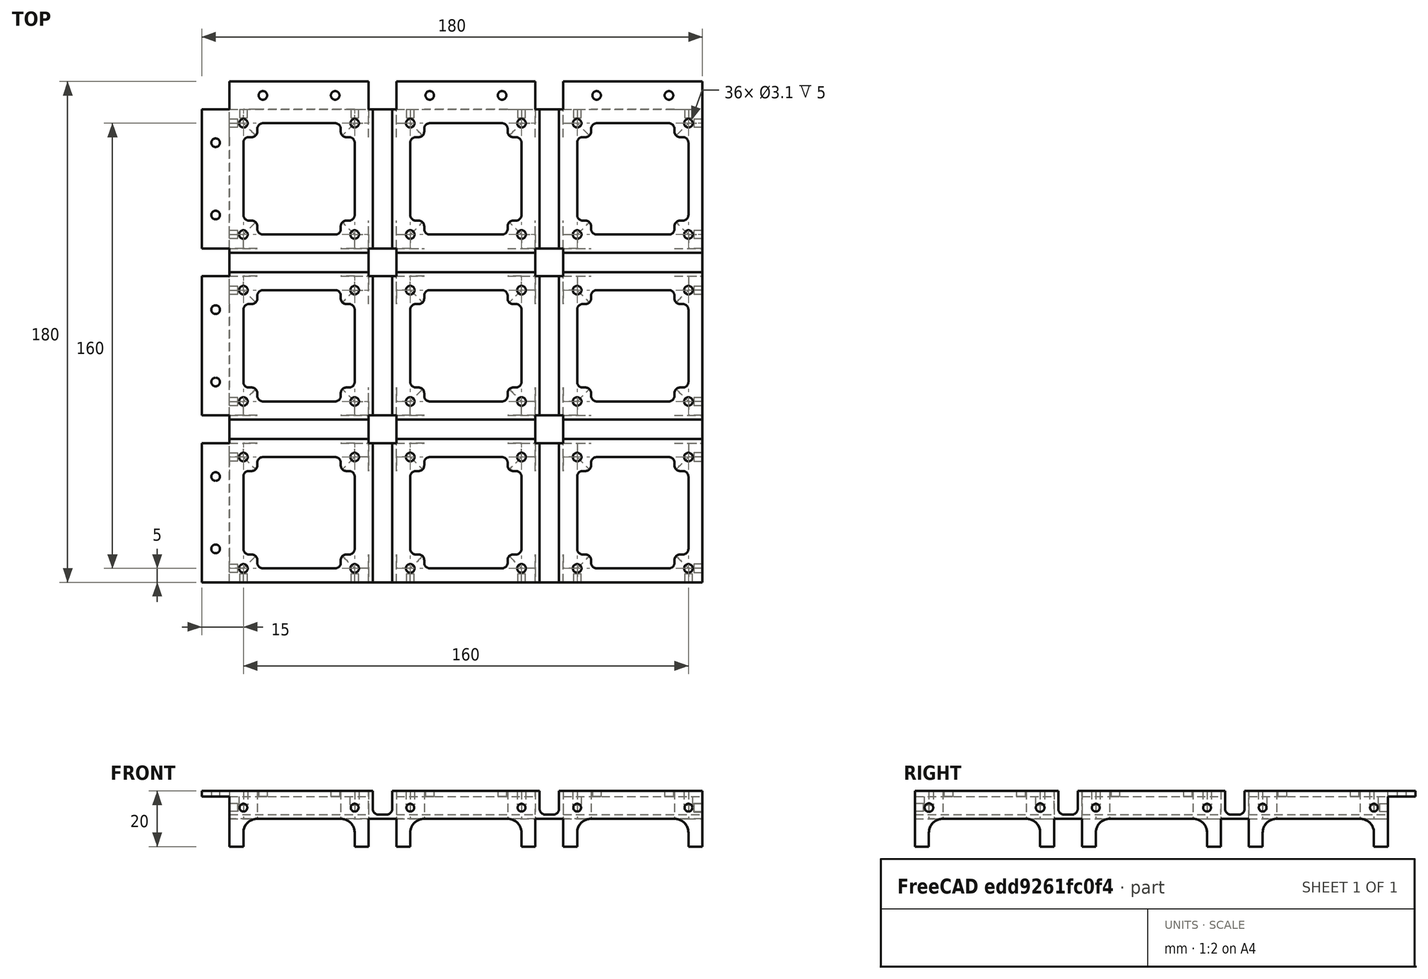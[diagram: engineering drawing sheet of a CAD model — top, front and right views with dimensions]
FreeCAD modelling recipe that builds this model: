
FCSTD DOCUMENT  (FreeCAD 0.20R29603 (Git))
Label: Backplane
License: All rights reserved
LicenseURL: http://en.wikipedia.org/wiki/All_rights_reserved
objects: Sketcher::SketchObject×59, PartDesign::Pocket×49, App::Link×16, PartDesign::Pad×10, PartDesign::Body×10, Part::Cylinder×2, Part::Cut×2, Part::Box×1, App::Part×1, Part::MultiFuse×1, Mesh::Feature×1
note: 193 computed .brp shape members not serialized (recipe doc carries the construction recipe); baked Part::Feature solids carry a one-line shape summary decoded from their .brp

FEATURE [Sketcher::SketchObject] Sketch
  FullyConstrained = true
  MapMode = 5
  Placement = pos=(0,0,0) rot=(0.57735,0.57735,0.57735;2.0944rad)
  Support = -> [YZ_Plane001]
  sketch-geometry (4):
    g0: LineSegment StartX=0 StartY=0 StartZ=0 EndX=10 EndY=0 EndZ=0
    g1: LineSegment StartX=10 StartY=0 StartZ=0 EndX=10 EndY=10 EndZ=0
    g2: LineSegment StartX=10 StartY=10 StartZ=0 EndX=0 EndY=10 EndZ=0
    g3: LineSegment StartX=0 StartY=10 StartZ=0 EndX=0 EndY=0 EndZ=0
  constraints (11):
    c: Coincident(g0,g1)
    c: Coincident(g1,g2)
    c: Coincident(g2,g3)
    c: Coincident(g3,g0)
    c: Horizontal(g0)
    c: Horizontal(g2)
    c: Vertical(g1)
    c: Vertical(g3)
    c: Coincident(g0,g-1)
    c: DistanceY(g3,g3) = 10
    c: DistanceX(g2,g2) = 10
FEATURE [PartDesign::Pad] Pad
  Direction = (1,-2e-16,3e-16)
  Length = 50
  Length2 = 10
  Placement = pos=(0,0,0) rot=(0.57735,0.57735,0.57735;2.0944rad)
  Profile = -> Sketch
  ReferenceAxis = -> Sketch [N_Axis]
  Type = 0
FEATURE [Sketcher::SketchObject] Sketch001
  ExternalGeometry = -> [Pad]
  FullyConstrained = true
  MapMode = 5
  Placement = pos=(0,0,0) rot=(0.57735,0.57735,-0.57735;4.18879rad)
  Support = -> [Pad]
  sketch-geometry (6):
    g0: LineSegment StartX=8.5 StartY=-10 StartZ=0 EndX=8.5 EndY=-3.5 EndZ=0
    g1: LineSegment StartX=6.5 StartY=-1.5 StartZ=0 EndX=3.5 EndY=-1.5 EndZ=0
    g2: LineSegment StartX=1.5 StartY=-3.5 StartZ=0 EndX=1.5 EndY=-10 EndZ=0
    g3: ArcOfCircle CenterX=6.5 CenterY=-3.5 CenterZ=0 NormalX=0 NormalY=0 NormalZ=1 AngleXU=0 Radius=2 StartAngle=1e-16 EndAngle=1.5708
    g4: ArcOfCircle CenterX=3.5 CenterY=-3.5 CenterZ=0 NormalX=0 NormalY=0 NormalZ=1 AngleXU=0 Radius=2 StartAngle=1.5708 EndAngle=3.14159
    g5: LineSegment StartX=1.5 StartY=-10 StartZ=0 EndX=8.5 EndY=-10 EndZ=0
  constraints (16):
    c: PointOnObject(g0,g-3)
    c: Vertical(g0)
    c: Horizontal(g1)
    c: PointOnObject(g2,g-3)
    c: Vertical(g2)
    c: Tangent(g0,g3) = -1.5708
    c: Tangent(g1,g3) = -1.5708
    c: Tangent(g1,g4) = -1.5708
    c: Tangent(g2,g4) = -1.5708
    c: Radius(g4) = 2
    c: Radius(g3) = 2
    c: Distance(g2,g-5) = 1.5
    c: Distance(g0,g-4) = 1.5
    c: Distance(g1,g-6) = 1.5
    c: Coincident(g5,g2)
    c: Coincident(g5,g0)
FEATURE [PartDesign::Pocket] Pocket
  BaseFeature = -> Pad
  Direction = (1,-4e-16,4e-16)
  Length = 5
  Length2 = 5
  Placement = pos=(0,0,0) rot=(0.57735,0.57735,0.57735;2.0944rad)
  Profile = -> Sketch001
  ReferenceAxis = -> Sketch001 [N_Axis]
  Type = 1
FEATURE [PartDesign::Body] Body  label="BackplaneChannel"
  Group = -> [Sketch,Pad,Sketch001,Pocket]
  Origin = -> Origin001
  Placement = pos=(0,50,10) rot=(0,0,1;0rad)
  Tip = -> Pocket
FEATURE [App::Link] Link008  label="BackplaneChannel001"
  LinkPlacement = pos=(60,50,10) rot=(0,0,1;0rad)
  LinkedObject = -> Body
  Placement = pos=(60,50,10) rot=(0,0,1;0rad)
FEATURE [App::Link] Link009  label="BackplaneChannel002"
  LinkPlacement = pos=(120,50,10) rot=(0,0,1;0rad)
  LinkedObject = -> Body
  Placement = pos=(120,50,10) rot=(0,0,1;0rad)
FEATURE [App::Link] Link010  label="BackplaneChannel003"
  LinkPlacement = pos=(0,110,10) rot=(0,0,1;0rad)
  LinkedObject = -> Body
  Placement = pos=(0,110,10) rot=(0,0,1;0rad)
FEATURE [App::Link] Link011  label="BackplaneChannel004"
  LinkPlacement = pos=(60,110,10) rot=(0,0,1;0rad)
  LinkedObject = -> Body
  Placement = pos=(60,110,10) rot=(0,0,1;0rad)
FEATURE [App::Link] Link012  label="BackplaneChannel005"
  LinkPlacement = pos=(120,110,10) rot=(0,0,1;0rad)
  LinkedObject = -> Body
  Placement = pos=(120,110,10) rot=(0,0,1;0rad)
FEATURE [App::Link] Link013  label="BackplaneChannel006"
  LinkPlacement = pos=(60,0,10) rot=(0,0,1;1.5708rad)
  LinkedObject = -> Body
  Placement = pos=(60,0,10) rot=(0,0,1;1.5708rad)
FEATURE [App::Link] Link014  label="BackplaneChannel007"
  LinkPlacement = pos=(120,0,10) rot=(0,0,1;1.5708rad)
  LinkedObject = -> Body
  Placement = pos=(120,0,10) rot=(0,0,1;1.5708rad)
FEATURE [App::Link] Link015  label="BackplaneChannel008"
  LinkPlacement = pos=(60,60,10) rot=(0,0,1;1.5708rad)
  LinkedObject = -> Body
  Placement = pos=(60,60,10) rot=(0,0,1;1.5708rad)
FEATURE [App::Link] Link016  label="BackplaneChannel009"
  LinkPlacement = pos=(60,120,10) rot=(0,0,1;1.5708rad)
  LinkedObject = -> Body
  Placement = pos=(60,120,10) rot=(0,0,1;1.5708rad)
FEATURE [App::Link] Link017  label="BackplaneChannel010"
  LinkPlacement = pos=(120,60,10) rot=(0,0,1;1.5708rad)
  LinkedObject = -> Body
  Placement = pos=(120,60,10) rot=(0,0,1;1.5708rad)
FEATURE [App::Link] Link018  label="BackplaneChannel011"
  LinkPlacement = pos=(120,120,10) rot=(0,0,1;1.5708rad)
  LinkedObject = -> Body
  Placement = pos=(120,120,10) rot=(0,0,1;1.5708rad)
FEATURE [Sketcher::SketchObject] Sketch002
  FullyConstrained = true
  MapMode = 5
  Support = -> [XY_Plane002]
  sketch-geometry (4):
    g0: LineSegment StartX=-25 StartY=25 StartZ=0 EndX=25 EndY=25 EndZ=0
    g1: LineSegment StartX=25 StartY=25 StartZ=0 EndX=25 EndY=-25 EndZ=0
    g2: LineSegment StartX=25 StartY=-25 StartZ=0 EndX=-25 EndY=-25 EndZ=0
    g3: LineSegment StartX=-25 StartY=-25 StartZ=0 EndX=-25 EndY=25 EndZ=0
  constraints (10):
    c: Coincident(g0,g1)
    c: Coincident(g1,g2)
    c: Coincident(g2,g3)
    c: Coincident(g3,g0)
    c: Horizontal(g0)
    c: Vertical(g3)
    c: Symmetric(g2,g1,g-2)
    c: Symmetric(g1,g0,g-1)
    c: DistanceY(g1,g1) = 50
    c: DistanceX(g2,g2) = 50
FEATURE [PartDesign::Pad] Pad001
  Direction = (0,0,1)
  Length = 20
  Length2 = 10
  Profile = -> Sketch002
  ReferenceAxis = -> Sketch002 [N_Axis]
  Type = 0
FEATURE [Sketcher::SketchObject] Sketch003
  ExternalGeometry = -> [Pad001]
  FullyConstrained = true
  MapMode = 5
  Placement = pos=(0,0,20) rot=(0,0,1;0rad)
  Support = -> [Pad001]
  sketch-geometry (36):
    g0: LineSegment StartX=-18 StartY=15 StartZ=0 EndX=-17 EndY=15 EndZ=0
    g1: LineSegment StartX=20 StartY=13 StartZ=0 EndX=20 EndY=-13 EndZ=0
    g2: LineSegment StartX=18 StartY=-15 StartZ=0 EndX=17 EndY=-15 EndZ=0
    g3: LineSegment StartX=-20 StartY=-13 StartZ=0 EndX=-20 EndY=13 EndZ=0
    g4: LineSegment StartX=-13 StartY=20 StartZ=0 EndX=13 EndY=20 EndZ=0
    g5: LineSegment StartX=15 StartY=18 StartZ=0 EndX=15 EndY=17 EndZ=0
    g6: LineSegment StartX=13 StartY=-20 StartZ=0 EndX=-13 EndY=-20 EndZ=0
    g7: LineSegment StartX=-15 StartY=-18 StartZ=0 EndX=-15 EndY=-17 EndZ=0
    g8: LineSegment StartX=17 StartY=15 StartZ=0 EndX=18 EndY=15 EndZ=0
    g9: LineSegment StartX=-15 StartY=17 StartZ=0 EndX=-15 EndY=18 EndZ=0
    g10: LineSegment StartX=-17 StartY=-15 StartZ=0 EndX=-18 EndY=-15 EndZ=0
    g11: LineSegment StartX=15 StartY=-17 StartZ=0 EndX=15 EndY=-18 EndZ=0
    g12: ArcOfCircle CenterX=-13 CenterY=-18 CenterZ=0 NormalX=0 NormalY=0 NormalZ=1 AngleXU=0 Radius=2 StartAngle=3.14159 EndAngle=4.71239
    g13: GeomPoint X=-15 Y=-20 Z=0
    g14: ArcOfCircle CenterX=13 CenterY=-18 CenterZ=0 NormalX=0 NormalY=0 NormalZ=1 AngleXU=0 Radius=2 StartAngle=4.71239 EndAngle=6.28319
    g15: GeomPoint X=15 Y=-20 Z=0
    g16: ArcOfCircle CenterX=17 CenterY=-17 CenterZ=0 NormalX=0 NormalY=0 NormalZ=1 AngleXU=0 Radius=2 StartAngle=1.5708 EndAngle=3.14159
    g17: GeomPoint X=15 Y=-15 Z=0
    g18: ArcOfCircle CenterX=18 CenterY=-13 CenterZ=0 NormalX=0 NormalY=0 NormalZ=1 AngleXU=0 Radius=2 StartAngle=4.71239 EndAngle=6.28319
    g19: GeomPoint X=20 Y=-15 Z=0
    g20: ArcOfCircle CenterX=18 CenterY=13 CenterZ=0 NormalX=0 NormalY=0 NormalZ=1 AngleXU=0 Radius=2 StartAngle=0 EndAngle=1.5708
    g21: GeomPoint X=20 Y=15 Z=0
    g22: ArcOfCircle CenterX=17 CenterY=17 CenterZ=0 NormalX=0 NormalY=0 NormalZ=1 AngleXU=0 Radius=2 StartAngle=3.14159 EndAngle=4.71239
    g23: GeomPoint X=15 Y=15 Z=0
    g24: ArcOfCircle CenterX=13 CenterY=18 CenterZ=0 NormalX=0 NormalY=0 NormalZ=1 AngleXU=0 Radius=2 StartAngle=4e-16 EndAngle=1.5708
    g25: GeomPoint X=15 Y=20 Z=0
    g26: ArcOfCircle CenterX=-13 CenterY=18 CenterZ=0 NormalX=0 NormalY=0 NormalZ=1 AngleXU=0 Radius=2 StartAngle=1.5708 EndAngle=3.14159
    g27: GeomPoint X=-15 Y=20 Z=0
    g28: ArcOfCircle CenterX=-17 CenterY=17 CenterZ=0 NormalX=0 NormalY=0 NormalZ=1 AngleXU=0 Radius=2 StartAngle=4.71239 EndAngle=6.28319
    g29: GeomPoint X=-15 Y=15 Z=0
    g30: ArcOfCircle CenterX=-18 CenterY=13 CenterZ=0 NormalX=0 NormalY=0 NormalZ=1 AngleXU=0 Radius=2 StartAngle=1.5708 EndAngle=3.14159
    g31: GeomPoint X=-20 Y=15 Z=0
    g32: ArcOfCircle CenterX=-18 CenterY=-13 CenterZ=0 NormalX=0 NormalY=0 NormalZ=1 AngleXU=0 Radius=2 StartAngle=3.14159 EndAngle=4.71239
    g33: GeomPoint X=-20 Y=-15 Z=0
    g34: ArcOfCircle CenterX=-17 CenterY=-17 CenterZ=0 NormalX=0 NormalY=0 NormalZ=1 AngleXU=0 Radius=2 StartAngle=0 EndAngle=1.5708
    g35: GeomPoint X=-15 Y=-15 Z=0
  constraints (80):
    c: Horizontal(g2)
    c: Vertical(g3)
    c: Symmetric(g21,g31,g-2)
    c: Symmetric(g21,g19,g-1)
    c: DistanceX(g31,g21) = 40
    c: DistanceY(g19,g21) = 30
    c: Horizontal(g4)
    c: Vertical(g7)
    c: Symmetric(g13,g15,g-2)
    c: Symmetric(g15,g25,g-1)
    c: DistanceY(g15,g25) = 40
    c: Vertical(g9)
    c: Vertical(g5)
    c: Vertical(g11)
    c: Horizontal(g10)
    c: Horizontal(g8)
    c: Horizontal(g0)
    c: DistanceX(g13,g15) = 30
    c: DistanceY(g33,g31) = 30
    c: DistanceX(g27,g25) = 30
    c: PointOnObject(g13,g7)
    c: PointOnObject(g13,g6)
    c: Tangent(g7,g12) = 1.5708
    c: Tangent(g6,g12) = 1.5708
    c: Radius(g12) = 2
    c: PointOnObject(g15,g11)
    c: PointOnObject(g15,g6)
    c: Tangent(g11,g14) = 1.5708
    c: Tangent(g6,g14) = 1.5708
    c: PointOnObject(g17,g11)
    c: PointOnObject(g17,g2)
    c: Tangent(g11,g16) = -1.5708
    c: Tangent(g2,g16) = -1.5708
    c: PointOnObject(g19,g2)
    c: PointOnObject(g19,g1)
    c: Tangent(g2,g18) = 1.5708
    c: Tangent(g1,g18) = 1.5708
    c: PointOnObject(g21,g1)
    c: PointOnObject(g21,g8)
    c: Tangent(g1,g20) = 1.5708
    c: Tangent(g8,g20) = 1.5708
    c: PointOnObject(g23,g8)
    c: PointOnObject(g23,g5)
    c: Tangent(g8,g22) = -1.5708
    c: Tangent(g5,g22) = -1.5708
    c: PointOnObject(g25,g5)
    c: PointOnObject(g25,g4)
    c: Tangent(g5,g24) = 1.5708
    c: Tangent(g4,g24) = 1.5708
    c: PointOnObject(g27,g9)
    c: PointOnObject(g27,g4)
    c: Tangent(g9,g26) = 1.5708
    c: Tangent(g4,g26) = 1.5708
    c: PointOnObject(g29,g9)
    c: PointOnObject(g29,g0)
    c: Tangent(g9,g28) = -1.5708
    c: Tangent(g0,g28) = -1.5708
    c: PointOnObject(g31,g0)
    c: PointOnObject(g31,g3)
    c: Tangent(g0,g30) = 1.5708
    c: Tangent(g3,g30) = 1.5708
    c: PointOnObject(g33,g3)
    c: PointOnObject(g33,g10)
    c: Tangent(g3,g32) = 1.5708
    c: Tangent(g10,g32) = 1.5708
    c: PointOnObject(g35,g10)
    c: PointOnObject(g35,g7)
    c: Tangent(g10,g34) = -1.5708
    c: Tangent(g7,g34) = -1.5708
    c: Radius(g34) = 2
    c: Radius(g32) = 2
    c: Radius(g30) = 2
    c: Radius(g28) = 2
    c: Radius(g26) = 2
    c: Radius(g24) = 2
    c: Radius(g22) = 2
    c: Radius(g20) = 2
    c: Radius(g18) = 2
    c: Radius(g16) = 2
    c: Radius(g14) = 2
FEATURE [PartDesign::Pocket] Pocket001
  BaseFeature = -> Pad001
  Direction = (0,0,-1)
  Length = 5
  Length2 = 5
  Profile = -> Sketch003
  ReferenceAxis = -> Sketch003 [N_Axis]
  Type = 1
FEATURE [Sketcher::SketchObject] Sketch004
  ExternalGeometry = -> [Pocket001]
  FullyConstrained = true
  MapMode = 5
  Placement = pos=(25,0,0) rot=(0.57735,0.57735,0.57735;2.0944rad)
  Support = -> [Pocket001]
  sketch-geometry (6):
    g0: LineSegment StartX=-15 StartY=10 StartZ=0 EndX=15 EndY=10 EndZ=0
    g1: LineSegment StartX=20 StartY=5 StartZ=0 EndX=20 EndY=0 EndZ=0
    g2: LineSegment StartX=20 StartY=0 StartZ=0 EndX=-20 EndY=0 EndZ=0
    g3: LineSegment StartX=-20 StartY=0 StartZ=0 EndX=-20 EndY=5 EndZ=0
    g4: ArcOfCircle CenterX=15 CenterY=5 CenterZ=0 NormalX=0 NormalY=0 NormalZ=1 AngleXU=0 Radius=5 StartAngle=1.11001e-11 EndAngle=1.5708
    g5: ArcOfCircle CenterX=-15 CenterY=5 CenterZ=0 NormalX=0 NormalY=0 NormalZ=1 AngleXU=0 Radius=5 StartAngle=1.5708 EndAngle=3.14159
  constraints (15):
    c: Coincident(g1,g2)
    c: Coincident(g2,g3)
    c: Vertical(g1)
    c: Vertical(g3)
    c: PointOnObject(g1,g-1)
    c: Tangent(g1,g4) = 1.5708
    c: Tangent(g0,g4) = 1.5708
    c: Tangent(g0,g5) = 1.5708
    c: Tangent(g3,g5) = 1.5708
    c: Horizontal(g0)
    c: DistanceX(g2,g2) = 40
    c: Symmetric(g2,g1,g-2)
    c: Distance(g-1,g0) = 10
    c: Radius(g5) = 5
    c: Radius(g4) = 5
FEATURE [PartDesign::Pocket] Pocket002
  BaseFeature = -> Pocket001
  Direction = (-1,0,0)
  Length = 5
  Length2 = 5
  Profile = -> Sketch004
  ReferenceAxis = -> Sketch004 [N_Axis]
  Type = 1
FEATURE [Sketcher::SketchObject] Sketch005
  FullyConstrained = true
  MapMode = 5
  Placement = pos=(0,-25,0) rot=(1,0,0;1.5708rad)
  Support = -> [Pocket001]
  sketch-geometry (6):
    g0: LineSegment StartX=-15 StartY=10 StartZ=0 EndX=15 EndY=10 EndZ=0
    g1: LineSegment StartX=20 StartY=5 StartZ=0 EndX=20 EndY=0 EndZ=0
    g2: LineSegment StartX=20 StartY=0 StartZ=0 EndX=-20 EndY=0 EndZ=0
    g3: LineSegment StartX=-20 StartY=0 StartZ=0 EndX=-20 EndY=5 EndZ=0
    g4: ArcOfCircle CenterX=15 CenterY=5 CenterZ=0 NormalX=0 NormalY=0 NormalZ=1 AngleXU=0 Radius=5 StartAngle=1.11e-11 EndAngle=1.5708
    g5: ArcOfCircle CenterX=-15 CenterY=5 CenterZ=0 NormalX=0 NormalY=0 NormalZ=1 AngleXU=0 Radius=5 StartAngle=1.5708 EndAngle=3.14159
  constraints (15):
    c: Coincident(g1,g2)
    c: Coincident(g2,g3)
    c: Horizontal(g0)
    c: Vertical(g1)
    c: Vertical(g3)
    c: Symmetric(g2,g1,g-2)
    c: PointOnObject(g1,g-1)
    c: Tangent(g0,g4) = 1.5708
    c: Tangent(g1,g4) = 1.5708
    c: Tangent(g0,g5) = 1.5708
    c: Tangent(g3,g5) = 1.5708
    c: DistanceX(g2,g2) = 40
    c: Distance(g-1,g0) = 10
    c: Radius(g5) = 5
    c: Radius(g4) = 5
FEATURE [PartDesign::Pocket] Pocket003
  BaseFeature = -> Pocket002
  Direction = (0,1,-2e-16)
  Length = 5
  Length2 = 5
  Profile = -> Sketch005
  ReferenceAxis = -> Sketch005 [N_Axis]
  Type = 1
FEATURE [Sketcher::SketchObject] Sketch009
  FullyConstrained = false
  MapMode = 5
  Placement = pos=(0,0,20) rot=(0,0,1;0rad)
  sketch-geometry (4):
    g0: Circle CenterX=-20 CenterY=20 CenterZ=0 NormalX=0 NormalY=0 NormalZ=1 AngleXU=0 Radius=1.55
    g1: Circle CenterX=20 CenterY=20 CenterZ=0 NormalX=0 NormalY=0 NormalZ=1 AngleXU=0 Radius=1.55
    g2: Circle CenterX=20 CenterY=-20 CenterZ=0 NormalX=0 NormalY=0 NormalZ=1 AngleXU=0 Radius=1.55
    g3: Circle CenterX=-20 CenterY=-20 CenterZ=0 NormalX=0 NormalY=0 NormalZ=1 AngleXU=0 Radius=1.55
  constraints (4):
    c: Diameter(g0) = 3.1
    c: Diameter(g1) = 3.1
    c: Diameter(g2) = 3.1
    c: Diameter(g3) = 3.1
FEATURE [PartDesign::Pocket] Pocket008
  BaseFeature = -> Pocket003
  Direction = (0,0,-1)
  Length = 5
  Length2 = 5
  Profile = -> Sketch009
  ReferenceAxis = -> Sketch009 [N_Axis]
  Type = 0
FEATURE [Sketcher::SketchObject] Sketch010
  FullyConstrained = true
  MapMode = 5
  Support = -> [XY_Plane003]
  sketch-geometry (4):
    g0: LineSegment StartX=-25 StartY=25 StartZ=0 EndX=25 EndY=25 EndZ=0
    g1: LineSegment StartX=25 StartY=25 StartZ=0 EndX=25 EndY=-25 EndZ=0
    g2: LineSegment StartX=25 StartY=-25 StartZ=0 EndX=-25 EndY=-25 EndZ=0
    g3: LineSegment StartX=-25 StartY=-25 StartZ=0 EndX=-25 EndY=25 EndZ=0
  constraints (10):
    c: Coincident(g0,g1)
    c: Coincident(g1,g2)
    c: Coincident(g2,g3)
    c: Coincident(g3,g0)
    c: Horizontal(g0)
    c: Vertical(g3)
    c: Symmetric(g2,g1,g-2)
    c: Symmetric(g1,g0,g-1)
    c: DistanceY(g1,g1) = 50
    c: DistanceX(g2,g2) = 50
FEATURE [PartDesign::Pad] Pad002
  Direction = (0,0,1)
  Length = 20
  Length2 = 10
  Profile = -> Sketch010
  ReferenceAxis = -> Sketch010 [N_Axis]
  Type = 0
FEATURE [Sketcher::SketchObject] Sketch011
  ExternalGeometry = -> [Pad002]
  FullyConstrained = true
  MapMode = 5
  Placement = pos=(0,0,20) rot=(0,0,1;0rad)
  Support = -> [Pad002]
  sketch-geometry (36):
    g0: LineSegment StartX=-18 StartY=15 StartZ=0 EndX=-17 EndY=15 EndZ=0
    g1: LineSegment StartX=20 StartY=13 StartZ=0 EndX=20 EndY=-13 EndZ=0
    g2: LineSegment StartX=18 StartY=-15 StartZ=0 EndX=17 EndY=-15 EndZ=0
    g3: LineSegment StartX=-20 StartY=-13 StartZ=0 EndX=-20 EndY=13 EndZ=0
    g4: LineSegment StartX=-13 StartY=20 StartZ=0 EndX=13 EndY=20 EndZ=0
    g5: LineSegment StartX=15 StartY=18 StartZ=0 EndX=15 EndY=17 EndZ=0
    g6: LineSegment StartX=13 StartY=-20 StartZ=0 EndX=-13 EndY=-20 EndZ=0
    g7: LineSegment StartX=-15 StartY=-18 StartZ=0 EndX=-15 EndY=-17 EndZ=0
    g8: LineSegment StartX=17 StartY=15 StartZ=0 EndX=18 EndY=15 EndZ=0
    g9: LineSegment StartX=-15 StartY=17 StartZ=0 EndX=-15 EndY=18 EndZ=0
    g10: LineSegment StartX=-17 StartY=-15 StartZ=0 EndX=-18 EndY=-15 EndZ=0
    g11: LineSegment StartX=15 StartY=-17 StartZ=0 EndX=15 EndY=-18 EndZ=0
    g12: ArcOfCircle CenterX=-13 CenterY=-18 CenterZ=0 NormalX=0 NormalY=0 NormalZ=1 AngleXU=0 Radius=2 StartAngle=3.14159 EndAngle=4.71239
    g13: GeomPoint X=-15 Y=-20 Z=0
    g14: ArcOfCircle CenterX=13 CenterY=-18 CenterZ=0 NormalX=0 NormalY=0 NormalZ=1 AngleXU=0 Radius=2 StartAngle=4.71239 EndAngle=6.28319
    g15: GeomPoint X=15 Y=-20 Z=0
    g16: ArcOfCircle CenterX=17 CenterY=-17 CenterZ=0 NormalX=0 NormalY=0 NormalZ=1 AngleXU=0 Radius=2 StartAngle=1.5708 EndAngle=3.14159
    g17: GeomPoint X=15 Y=-15 Z=0
    g18: ArcOfCircle CenterX=18 CenterY=-13 CenterZ=0 NormalX=0 NormalY=0 NormalZ=1 AngleXU=0 Radius=2 StartAngle=4.71239 EndAngle=6.28319
    g19: GeomPoint X=20 Y=-15 Z=0
    g20: ArcOfCircle CenterX=18 CenterY=13 CenterZ=0 NormalX=0 NormalY=0 NormalZ=1 AngleXU=0 Radius=2 StartAngle=0 EndAngle=1.5708
    g21: GeomPoint X=20 Y=15 Z=0
    g22: ArcOfCircle CenterX=17 CenterY=17 CenterZ=0 NormalX=0 NormalY=0 NormalZ=1 AngleXU=0 Radius=2 StartAngle=3.14159 EndAngle=4.71239
    g23: GeomPoint X=15 Y=15 Z=0
    g24: ArcOfCircle CenterX=13 CenterY=18 CenterZ=0 NormalX=0 NormalY=0 NormalZ=1 AngleXU=0 Radius=2 StartAngle=4e-16 EndAngle=1.5708
    g25: GeomPoint X=15 Y=20 Z=0
    g26: ArcOfCircle CenterX=-13 CenterY=18 CenterZ=0 NormalX=0 NormalY=0 NormalZ=1 AngleXU=0 Radius=2 StartAngle=1.5708 EndAngle=3.14159
    g27: GeomPoint X=-15 Y=20 Z=0
    g28: ArcOfCircle CenterX=-17 CenterY=17 CenterZ=0 NormalX=0 NormalY=0 NormalZ=1 AngleXU=0 Radius=2 StartAngle=4.71239 EndAngle=6.28319
    g29: GeomPoint X=-15 Y=15 Z=0
    g30: ArcOfCircle CenterX=-18 CenterY=13 CenterZ=0 NormalX=0 NormalY=0 NormalZ=1 AngleXU=0 Radius=2 StartAngle=1.5708 EndAngle=3.14159
    g31: GeomPoint X=-20 Y=15 Z=0
    g32: ArcOfCircle CenterX=-18 CenterY=-13 CenterZ=0 NormalX=0 NormalY=0 NormalZ=1 AngleXU=0 Radius=2 StartAngle=3.14159 EndAngle=4.71239
    g33: GeomPoint X=-20 Y=-15 Z=0
    g34: ArcOfCircle CenterX=-17 CenterY=-17 CenterZ=0 NormalX=0 NormalY=0 NormalZ=1 AngleXU=0 Radius=2 StartAngle=0 EndAngle=1.5708
    g35: GeomPoint X=-15 Y=-15 Z=0
  constraints (80):
    c: Horizontal(g2)
    c: Vertical(g3)
    c: Symmetric(g21,g31,g-2)
    c: Symmetric(g21,g19,g-1)
    c: DistanceX(g31,g21) = 40
    c: DistanceY(g19,g21) = 30
    c: Horizontal(g4)
    c: Vertical(g7)
    c: Symmetric(g13,g15,g-2)
    c: Symmetric(g15,g25,g-1)
    c: DistanceY(g15,g25) = 40
    c: Vertical(g9)
    c: Vertical(g5)
    c: Vertical(g11)
    c: Horizontal(g10)
    c: Horizontal(g8)
    c: Horizontal(g0)
    c: DistanceX(g13,g15) = 30
    c: DistanceY(g33,g31) = 30
    c: DistanceX(g27,g25) = 30
    c: PointOnObject(g13,g7)
    c: PointOnObject(g13,g6)
    c: Tangent(g7,g12) = 1.5708
    c: Tangent(g6,g12) = 1.5708
    c: Radius(g12) = 2
    c: PointOnObject(g15,g11)
    c: PointOnObject(g15,g6)
    c: Tangent(g11,g14) = 1.5708
    c: Tangent(g6,g14) = 1.5708
    c: PointOnObject(g17,g11)
    c: PointOnObject(g17,g2)
    c: Tangent(g11,g16) = -1.5708
    c: Tangent(g2,g16) = -1.5708
    c: PointOnObject(g19,g2)
    c: PointOnObject(g19,g1)
    c: Tangent(g2,g18) = 1.5708
    c: Tangent(g1,g18) = 1.5708
    c: PointOnObject(g21,g1)
    c: PointOnObject(g21,g8)
    c: Tangent(g1,g20) = 1.5708
    c: Tangent(g8,g20) = 1.5708
    c: PointOnObject(g23,g8)
    c: PointOnObject(g23,g5)
    c: Tangent(g8,g22) = -1.5708
    c: Tangent(g5,g22) = -1.5708
    c: PointOnObject(g25,g5)
    c: PointOnObject(g25,g4)
    c: Tangent(g5,g24) = 1.5708
    c: Tangent(g4,g24) = 1.5708
    c: PointOnObject(g27,g9)
    c: PointOnObject(g27,g4)
    c: Tangent(g9,g26) = 1.5708
    c: Tangent(g4,g26) = 1.5708
    c: PointOnObject(g29,g9)
    c: PointOnObject(g29,g0)
    c: Tangent(g9,g28) = -1.5708
    c: Tangent(g0,g28) = -1.5708
    c: PointOnObject(g31,g0)
    c: PointOnObject(g31,g3)
    c: Tangent(g0,g30) = 1.5708
    c: Tangent(g3,g30) = 1.5708
    c: PointOnObject(g33,g3)
    c: PointOnObject(g33,g10)
    c: Tangent(g3,g32) = 1.5708
    c: Tangent(g10,g32) = 1.5708
    c: PointOnObject(g35,g10)
    c: PointOnObject(g35,g7)
    c: Tangent(g10,g34) = -1.5708
    c: Tangent(g7,g34) = -1.5708
    c: Radius(g34) = 2
    c: Radius(g32) = 2
    c: Radius(g30) = 2
    c: Radius(g28) = 2
    c: Radius(g26) = 2
    c: Radius(g24) = 2
    c: Radius(g22) = 2
    c: Radius(g20) = 2
    c: Radius(g18) = 2
    c: Radius(g16) = 2
    c: Radius(g14) = 2
FEATURE [PartDesign::Pocket] Pocket009
  BaseFeature = -> Pad002
  Direction = (0,0,-1)
  Length = 5
  Length2 = 5
  Profile = -> Sketch011
  ReferenceAxis = -> Sketch011 [N_Axis]
  Type = 1
FEATURE [Sketcher::SketchObject] Sketch012
  ExternalGeometry = -> [Pocket009]
  FullyConstrained = true
  MapMode = 5
  Placement = pos=(25,0,0) rot=(0.57735,0.57735,0.57735;2.0944rad)
  Support = -> [Pocket009]
  sketch-geometry (6):
    g0: LineSegment StartX=-15 StartY=10 StartZ=0 EndX=15 EndY=10 EndZ=0
    g1: LineSegment StartX=20 StartY=5 StartZ=0 EndX=20 EndY=0 EndZ=0
    g2: LineSegment StartX=20 StartY=0 StartZ=0 EndX=-20 EndY=0 EndZ=0
    g3: LineSegment StartX=-20 StartY=0 StartZ=0 EndX=-20 EndY=5 EndZ=0
    g4: ArcOfCircle CenterX=15 CenterY=5 CenterZ=0 NormalX=0 NormalY=0 NormalZ=1 AngleXU=0 Radius=5 StartAngle=1.11001e-11 EndAngle=1.5708
    g5: ArcOfCircle CenterX=-15 CenterY=5 CenterZ=0 NormalX=0 NormalY=0 NormalZ=1 AngleXU=0 Radius=5 StartAngle=1.5708 EndAngle=3.14159
  constraints (15):
    c: Coincident(g1,g2)
    c: Coincident(g2,g3)
    c: Vertical(g1)
    c: Vertical(g3)
    c: PointOnObject(g1,g-1)
    c: Tangent(g1,g4) = 1.5708
    c: Tangent(g0,g4) = 1.5708
    c: Tangent(g0,g5) = 1.5708
    c: Tangent(g3,g5) = 1.5708
    c: Horizontal(g0)
    c: DistanceX(g2,g2) = 40
    c: Symmetric(g2,g1,g-2)
    c: Distance(g-1,g0) = 10
    c: Radius(g5) = 5
    c: Radius(g4) = 5
FEATURE [PartDesign::Pocket] Pocket010
  BaseFeature = -> Pocket009
  Direction = (-1,0,0)
  Length = 5
  Length2 = 5
  Profile = -> Sketch012
  ReferenceAxis = -> Sketch012 [N_Axis]
  Type = 1
FEATURE [Sketcher::SketchObject] Sketch013
  FullyConstrained = true
  MapMode = 5
  Placement = pos=(0,-25,0) rot=(1,0,0;1.5708rad)
  Support = -> [Pocket009]
  sketch-geometry (6):
    g0: LineSegment StartX=-15 StartY=10 StartZ=0 EndX=15 EndY=10 EndZ=0
    g1: LineSegment StartX=20 StartY=5 StartZ=0 EndX=20 EndY=0 EndZ=0
    g2: LineSegment StartX=20 StartY=0 StartZ=0 EndX=-20 EndY=0 EndZ=0
    g3: LineSegment StartX=-20 StartY=0 StartZ=0 EndX=-20 EndY=5 EndZ=0
    g4: ArcOfCircle CenterX=15 CenterY=5 CenterZ=0 NormalX=0 NormalY=0 NormalZ=1 AngleXU=0 Radius=5 StartAngle=1.11e-11 EndAngle=1.5708
    g5: ArcOfCircle CenterX=-15 CenterY=5 CenterZ=0 NormalX=0 NormalY=0 NormalZ=1 AngleXU=0 Radius=5 StartAngle=1.5708 EndAngle=3.14159
  constraints (15):
    c: Coincident(g1,g2)
    c: Coincident(g2,g3)
    c: Horizontal(g0)
    c: Vertical(g1)
    c: Vertical(g3)
    c: Symmetric(g2,g1,g-2)
    c: PointOnObject(g1,g-1)
    c: Tangent(g0,g4) = 1.5708
    c: Tangent(g1,g4) = 1.5708
    c: Tangent(g0,g5) = 1.5708
    c: Tangent(g3,g5) = 1.5708
    c: DistanceX(g2,g2) = 40
    c: Distance(g-1,g0) = 10
    c: Radius(g5) = 5
    c: Radius(g4) = 5
FEATURE [PartDesign::Pocket] Pocket011
  BaseFeature = -> Pocket010
  Direction = (0,1,-2e-16)
  Length = 5
  Length2 = 5
  Profile = -> Sketch013
  ReferenceAxis = -> Sketch013 [N_Axis]
  Type = 1
FEATURE [Sketcher::SketchObject] Sketch014
  FullyConstrained = false
  MapMode = 5
  Placement = pos=(0,0,20) rot=(0,0,1;0rad)
  sketch-geometry (4):
    g0: Circle CenterX=-20 CenterY=20 CenterZ=0 NormalX=0 NormalY=0 NormalZ=1 AngleXU=0 Radius=1.55
    g1: Circle CenterX=20 CenterY=20 CenterZ=0 NormalX=0 NormalY=0 NormalZ=1 AngleXU=0 Radius=1.55
    g2: Circle CenterX=20 CenterY=-20 CenterZ=0 NormalX=0 NormalY=0 NormalZ=1 AngleXU=0 Radius=1.55
    g3: Circle CenterX=-20 CenterY=-20 CenterZ=0 NormalX=0 NormalY=0 NormalZ=1 AngleXU=0 Radius=1.55
  constraints (4):
    c: Diameter(g0) = 3.1
    c: Diameter(g1) = 3.1
    c: Diameter(g2) = 3.1
    c: Diameter(g3) = 3.1
FEATURE [PartDesign::Pocket] Pocket012
  BaseFeature = -> Pocket011
  Direction = (0,0,-1)
  Length = 5
  Length2 = 5
  Profile = -> Sketch014
  ReferenceAxis = -> Sketch014 [N_Axis]
  Type = 0
FEATURE [PartDesign::Body] Body003  label="BackplaneBlock001"
  Group = -> [Sketch010,Pad002,Sketch011,Pocket009,Sketch012,Sketch013,Pocket010,Pocket011,Sketch014,Pocket012]
  Origin = -> Origin003
  Placement = pos=(85,85,0) rot=(0,0,1;0rad)
  Tip = -> Pocket012
FEATURE [Sketcher::SketchObject] Sketch015
  ExternalGeometry = -> [Pocket008]
  FullyConstrained = true
  MapMode = 5
  Placement = pos=(0,-25,0) rot=(1,0,0;1.5708rad)
  Support = -> [Pocket008]
  sketch-geometry (2):
    g0: Circle CenterX=-20 CenterY=14 CenterZ=0 NormalX=0 NormalY=0 NormalZ=1 AngleXU=0 Radius=1.4
    g1: Circle CenterX=20 CenterY=14 CenterZ=0 NormalX=0 NormalY=0 NormalZ=1 AngleXU=0 Radius=1.4
  constraints (6):
    c: Diameter(g0) = 2.8
    c: Diameter(g1) = 2.8
    c: Distance(g0,g-5) = 5
    c: Distance(g0,g-3) = 6
    c: Distance(g1,g-3) = 6
    c: Distance(g1,g-4) = 5
FEATURE [PartDesign::Pocket] Pocket013
  BaseFeature = -> Pocket008
  Direction = (0,1,-2e-16)
  Length = 3
  Length2 = 5
  Profile = -> Sketch015
  ReferenceAxis = -> Sketch015 [N_Axis]
  Type = 0
FEATURE [Sketcher::SketchObject] Sketch016
  FullyConstrained = true
  MapMode = 5
  Support = -> [XY_Plane004]
  sketch-geometry (4):
    g0: LineSegment StartX=-25 StartY=25 StartZ=0 EndX=25 EndY=25 EndZ=0
    g1: LineSegment StartX=25 StartY=25 StartZ=0 EndX=25 EndY=-25 EndZ=0
    g2: LineSegment StartX=25 StartY=-25 StartZ=0 EndX=-25 EndY=-25 EndZ=0
    g3: LineSegment StartX=-25 StartY=-25 StartZ=0 EndX=-25 EndY=25 EndZ=0
  constraints (10):
    c: Coincident(g0,g1)
    c: Coincident(g1,g2)
    c: Coincident(g2,g3)
    c: Coincident(g3,g0)
    c: Horizontal(g0)
    c: Vertical(g3)
    c: Symmetric(g2,g1,g-2)
    c: Symmetric(g1,g0,g-1)
    c: DistanceY(g1,g1) = 50
    c: DistanceX(g2,g2) = 50
FEATURE [PartDesign::Pad] Pad003
  Direction = (0,0,1)
  Length = 20
  Length2 = 10
  Profile = -> Sketch016
  ReferenceAxis = -> Sketch016 [N_Axis]
  Type = 0
FEATURE [Sketcher::SketchObject] Sketch017
  ExternalGeometry = -> [Pad003]
  FullyConstrained = true
  MapMode = 5
  Placement = pos=(0,0,20) rot=(0,0,1;0rad)
  Support = -> [Pad003]
  sketch-geometry (36):
    g0: LineSegment StartX=-18 StartY=15 StartZ=0 EndX=-17 EndY=15 EndZ=0
    g1: LineSegment StartX=20 StartY=13 StartZ=0 EndX=20 EndY=-13 EndZ=0
    g2: LineSegment StartX=18 StartY=-15 StartZ=0 EndX=17 EndY=-15 EndZ=0
    g3: LineSegment StartX=-20 StartY=-13 StartZ=0 EndX=-20 EndY=13 EndZ=0
    g4: LineSegment StartX=-13 StartY=20 StartZ=0 EndX=13 EndY=20 EndZ=0
    g5: LineSegment StartX=15 StartY=18 StartZ=0 EndX=15 EndY=17 EndZ=0
    g6: LineSegment StartX=13 StartY=-20 StartZ=0 EndX=-13 EndY=-20 EndZ=0
    g7: LineSegment StartX=-15 StartY=-18 StartZ=0 EndX=-15 EndY=-17 EndZ=0
    g8: LineSegment StartX=17 StartY=15 StartZ=0 EndX=18 EndY=15 EndZ=0
    g9: LineSegment StartX=-15 StartY=17 StartZ=0 EndX=-15 EndY=18 EndZ=0
    g10: LineSegment StartX=-17 StartY=-15 StartZ=0 EndX=-18 EndY=-15 EndZ=0
    g11: LineSegment StartX=15 StartY=-17 StartZ=0 EndX=15 EndY=-18 EndZ=0
    g12: ArcOfCircle CenterX=-13 CenterY=-18 CenterZ=0 NormalX=0 NormalY=0 NormalZ=1 AngleXU=0 Radius=2 StartAngle=3.14159 EndAngle=4.71239
    g13: GeomPoint X=-15 Y=-20 Z=0
    g14: ArcOfCircle CenterX=13 CenterY=-18 CenterZ=0 NormalX=0 NormalY=0 NormalZ=1 AngleXU=0 Radius=2 StartAngle=4.71239 EndAngle=6.28319
    g15: GeomPoint X=15 Y=-20 Z=0
    g16: ArcOfCircle CenterX=17 CenterY=-17 CenterZ=0 NormalX=0 NormalY=0 NormalZ=1 AngleXU=0 Radius=2 StartAngle=1.5708 EndAngle=3.14159
    g17: GeomPoint X=15 Y=-15 Z=0
    g18: ArcOfCircle CenterX=18 CenterY=-13 CenterZ=0 NormalX=0 NormalY=0 NormalZ=1 AngleXU=0 Radius=2 StartAngle=4.71239 EndAngle=6.28319
    g19: GeomPoint X=20 Y=-15 Z=0
    g20: ArcOfCircle CenterX=18 CenterY=13 CenterZ=0 NormalX=0 NormalY=0 NormalZ=1 AngleXU=0 Radius=2 StartAngle=0 EndAngle=1.5708
    g21: GeomPoint X=20 Y=15 Z=0
    g22: ArcOfCircle CenterX=17 CenterY=17 CenterZ=0 NormalX=0 NormalY=0 NormalZ=1 AngleXU=0 Radius=2 StartAngle=3.14159 EndAngle=4.71239
    g23: GeomPoint X=15 Y=15 Z=0
    g24: ArcOfCircle CenterX=13 CenterY=18 CenterZ=0 NormalX=0 NormalY=0 NormalZ=1 AngleXU=0 Radius=2 StartAngle=4e-16 EndAngle=1.5708
    g25: GeomPoint X=15 Y=20 Z=0
    g26: ArcOfCircle CenterX=-13 CenterY=18 CenterZ=0 NormalX=0 NormalY=0 NormalZ=1 AngleXU=0 Radius=2 StartAngle=1.5708 EndAngle=3.14159
    g27: GeomPoint X=-15 Y=20 Z=0
    g28: ArcOfCircle CenterX=-17 CenterY=17 CenterZ=0 NormalX=0 NormalY=0 NormalZ=1 AngleXU=0 Radius=2 StartAngle=4.71239 EndAngle=6.28319
    g29: GeomPoint X=-15 Y=15 Z=0
    g30: ArcOfCircle CenterX=-18 CenterY=13 CenterZ=0 NormalX=0 NormalY=0 NormalZ=1 AngleXU=0 Radius=2 StartAngle=1.5708 EndAngle=3.14159
    g31: GeomPoint X=-20 Y=15 Z=0
    g32: ArcOfCircle CenterX=-18 CenterY=-13 CenterZ=0 NormalX=0 NormalY=0 NormalZ=1 AngleXU=0 Radius=2 StartAngle=3.14159 EndAngle=4.71239
    g33: GeomPoint X=-20 Y=-15 Z=0
    g34: ArcOfCircle CenterX=-17 CenterY=-17 CenterZ=0 NormalX=0 NormalY=0 NormalZ=1 AngleXU=0 Radius=2 StartAngle=0 EndAngle=1.5708
    g35: GeomPoint X=-15 Y=-15 Z=0
  constraints (80):
    c: Horizontal(g2)
    c: Vertical(g3)
    c: Symmetric(g21,g31,g-2)
    c: Symmetric(g21,g19,g-1)
    c: DistanceX(g31,g21) = 40
    c: DistanceY(g19,g21) = 30
    c: Horizontal(g4)
    c: Vertical(g7)
    c: Symmetric(g13,g15,g-2)
    c: Symmetric(g15,g25,g-1)
    c: DistanceY(g15,g25) = 40
    c: Vertical(g9)
    c: Vertical(g5)
    c: Vertical(g11)
    c: Horizontal(g10)
    c: Horizontal(g8)
    c: Horizontal(g0)
    c: DistanceX(g13,g15) = 30
    c: DistanceY(g33,g31) = 30
    c: DistanceX(g27,g25) = 30
    c: PointOnObject(g13,g7)
    c: PointOnObject(g13,g6)
    c: Tangent(g7,g12) = 1.5708
    c: Tangent(g6,g12) = 1.5708
    c: Radius(g12) = 2
    c: PointOnObject(g15,g11)
    c: PointOnObject(g15,g6)
    c: Tangent(g11,g14) = 1.5708
    c: Tangent(g6,g14) = 1.5708
    c: PointOnObject(g17,g11)
    c: PointOnObject(g17,g2)
    c: Tangent(g11,g16) = -1.5708
    c: Tangent(g2,g16) = -1.5708
    c: PointOnObject(g19,g2)
    c: PointOnObject(g19,g1)
    c: Tangent(g2,g18) = 1.5708
    c: Tangent(g1,g18) = 1.5708
    c: PointOnObject(g21,g1)
    c: PointOnObject(g21,g8)
    c: Tangent(g1,g20) = 1.5708
    c: Tangent(g8,g20) = 1.5708
    c: PointOnObject(g23,g8)
    c: PointOnObject(g23,g5)
    c: Tangent(g8,g22) = -1.5708
    c: Tangent(g5,g22) = -1.5708
    c: PointOnObject(g25,g5)
    c: PointOnObject(g25,g4)
    c: Tangent(g5,g24) = 1.5708
    c: Tangent(g4,g24) = 1.5708
    c: PointOnObject(g27,g9)
    c: PointOnObject(g27,g4)
    c: Tangent(g9,g26) = 1.5708
    c: Tangent(g4,g26) = 1.5708
    c: PointOnObject(g29,g9)
    c: PointOnObject(g29,g0)
    c: Tangent(g9,g28) = -1.5708
    c: Tangent(g0,g28) = -1.5708
    c: PointOnObject(g31,g0)
    c: PointOnObject(g31,g3)
    c: Tangent(g0,g30) = 1.5708
    c: Tangent(g3,g30) = 1.5708
    c: PointOnObject(g33,g3)
    c: PointOnObject(g33,g10)
    c: Tangent(g3,g32) = 1.5708
    c: Tangent(g10,g32) = 1.5708
    c: PointOnObject(g35,g10)
    c: PointOnObject(g35,g7)
    c: Tangent(g10,g34) = -1.5708
    c: Tangent(g7,g34) = -1.5708
    c: Radius(g34) = 2
    c: Radius(g32) = 2
    c: Radius(g30) = 2
    c: Radius(g28) = 2
    c: Radius(g26) = 2
    c: Radius(g24) = 2
    c: Radius(g22) = 2
    c: Radius(g20) = 2
    c: Radius(g18) = 2
    c: Radius(g16) = 2
    c: Radius(g14) = 2
FEATURE [PartDesign::Pocket] Pocket014
  BaseFeature = -> Pad003
  Direction = (0,0,-1)
  Length = 5
  Length2 = 5
  Profile = -> Sketch017
  ReferenceAxis = -> Sketch017 [N_Axis]
  Type = 1
FEATURE [Sketcher::SketchObject] Sketch018
  ExternalGeometry = -> [Pocket014]
  FullyConstrained = true
  MapMode = 5
  Placement = pos=(25,0,0) rot=(0.57735,0.57735,0.57735;2.0944rad)
  Support = -> [Pocket014]
  sketch-geometry (6):
    g0: LineSegment StartX=-15 StartY=10 StartZ=0 EndX=15 EndY=10 EndZ=0
    g1: LineSegment StartX=20 StartY=5 StartZ=0 EndX=20 EndY=0 EndZ=0
    g2: LineSegment StartX=20 StartY=0 StartZ=0 EndX=-20 EndY=0 EndZ=0
    g3: LineSegment StartX=-20 StartY=0 StartZ=0 EndX=-20 EndY=5 EndZ=0
    g4: ArcOfCircle CenterX=15 CenterY=5 CenterZ=0 NormalX=0 NormalY=0 NormalZ=1 AngleXU=0 Radius=5 StartAngle=1.11001e-11 EndAngle=1.5708
    g5: ArcOfCircle CenterX=-15 CenterY=5 CenterZ=0 NormalX=0 NormalY=0 NormalZ=1 AngleXU=0 Radius=5 StartAngle=1.5708 EndAngle=3.14159
  constraints (15):
    c: Coincident(g1,g2)
    c: Coincident(g2,g3)
    c: Vertical(g1)
    c: Vertical(g3)
    c: PointOnObject(g1,g-1)
    c: Tangent(g1,g4) = 1.5708
    c: Tangent(g0,g4) = 1.5708
    c: Tangent(g0,g5) = 1.5708
    c: Tangent(g3,g5) = 1.5708
    c: Horizontal(g0)
    c: DistanceX(g2,g2) = 40
    c: Symmetric(g2,g1,g-2)
    c: Distance(g-1,g0) = 10
    c: Radius(g5) = 5
    c: Radius(g4) = 5
FEATURE [PartDesign::Pocket] Pocket015
  BaseFeature = -> Pocket014
  Direction = (-1,0,0)
  Length = 5
  Length2 = 5
  Profile = -> Sketch018
  ReferenceAxis = -> Sketch018 [N_Axis]
  Type = 1
FEATURE [Sketcher::SketchObject] Sketch019
  FullyConstrained = true
  MapMode = 5
  Placement = pos=(0,-25,0) rot=(1,0,0;1.5708rad)
  Support = -> [Pocket014]
  sketch-geometry (6):
    g0: LineSegment StartX=-15 StartY=10 StartZ=0 EndX=15 EndY=10 EndZ=0
    g1: LineSegment StartX=20 StartY=5 StartZ=0 EndX=20 EndY=0 EndZ=0
    g2: LineSegment StartX=20 StartY=0 StartZ=0 EndX=-20 EndY=0 EndZ=0
    g3: LineSegment StartX=-20 StartY=0 StartZ=0 EndX=-20 EndY=5 EndZ=0
    g4: ArcOfCircle CenterX=15 CenterY=5 CenterZ=0 NormalX=0 NormalY=0 NormalZ=1 AngleXU=0 Radius=5 StartAngle=1.11e-11 EndAngle=1.5708
    g5: ArcOfCircle CenterX=-15 CenterY=5 CenterZ=0 NormalX=0 NormalY=0 NormalZ=1 AngleXU=0 Radius=5 StartAngle=1.5708 EndAngle=3.14159
  constraints (15):
    c: Coincident(g1,g2)
    c: Coincident(g2,g3)
    c: Horizontal(g0)
    c: Vertical(g1)
    c: Vertical(g3)
    c: Symmetric(g2,g1,g-2)
    c: PointOnObject(g1,g-1)
    c: Tangent(g0,g4) = 1.5708
    c: Tangent(g1,g4) = 1.5708
    c: Tangent(g0,g5) = 1.5708
    c: Tangent(g3,g5) = 1.5708
    c: DistanceX(g2,g2) = 40
    c: Distance(g-1,g0) = 10
    c: Radius(g5) = 5
    c: Radius(g4) = 5
FEATURE [PartDesign::Pocket] Pocket016
  BaseFeature = -> Pocket015
  Direction = (0,1,-2e-16)
  Length = 5
  Length2 = 5
  Profile = -> Sketch019
  ReferenceAxis = -> Sketch019 [N_Axis]
  Type = 1
FEATURE [Sketcher::SketchObject] Sketch020
  FullyConstrained = false
  MapMode = 5
  Placement = pos=(0,0,20) rot=(0,0,1;0rad)
  sketch-geometry (4):
    g0: Circle CenterX=-20 CenterY=20 CenterZ=0 NormalX=0 NormalY=0 NormalZ=1 AngleXU=0 Radius=1.55
    g1: Circle CenterX=20 CenterY=20 CenterZ=0 NormalX=0 NormalY=0 NormalZ=1 AngleXU=0 Radius=1.55
    g2: Circle CenterX=20 CenterY=-20 CenterZ=0 NormalX=0 NormalY=0 NormalZ=1 AngleXU=0 Radius=1.55
    g3: Circle CenterX=-20 CenterY=-20 CenterZ=0 NormalX=0 NormalY=0 NormalZ=1 AngleXU=0 Radius=1.55
  constraints (4):
    c: Diameter(g0) = 3.1
    c: Diameter(g1) = 3.1
    c: Diameter(g2) = 3.1
    c: Diameter(g3) = 3.1
FEATURE [PartDesign::Pocket] Pocket017
  BaseFeature = -> Pocket016
  Direction = (0,0,-1)
  Length = 5
  Length2 = 5
  Profile = -> Sketch020
  ReferenceAxis = -> Sketch020 [N_Axis]
  Type = 0
FEATURE [Sketcher::SketchObject] Sketch021
  ExternalGeometry = -> [Pocket017]
  FullyConstrained = true
  MapMode = 5
  Placement = pos=(0,-25,0) rot=(1,0,0;1.5708rad)
  Support = -> [Pocket017]
  sketch-geometry (2):
    g0: Circle CenterX=-20 CenterY=14 CenterZ=0 NormalX=0 NormalY=0 NormalZ=1 AngleXU=0 Radius=1.4
    g1: Circle CenterX=20 CenterY=14 CenterZ=0 NormalX=0 NormalY=0 NormalZ=1 AngleXU=0 Radius=1.4
  constraints (6):
    c: Diameter(g0) = 2.8
    c: Diameter(g1) = 2.8
    c: Distance(g0,g-5) = 5
    c: Distance(g0,g-3) = 6
    c: Distance(g1,g-3) = 6
    c: Distance(g1,g-4) = 5
FEATURE [PartDesign::Pocket] Pocket018
  BaseFeature = -> Pocket017
  Direction = (0,1,-2e-16)
  Length = 3
  Length2 = 5
  Profile = -> Sketch021
  ReferenceAxis = -> Sketch021 [N_Axis]
  Type = 0
FEATURE [PartDesign::Body] Body004  label="BackplaneBlock002"
  Group = -> [Sketch016,Pad003,Sketch017,Pocket014,Sketch018,Sketch019,Pocket015,Pocket016,Sketch020,Pocket017,Sketch021,Pocket018]
  Origin = -> Origin004
  Placement = pos=(85,145,0) rot=(0,0,1;3.14159rad)
  Tip = -> Pocket018
FEATURE [Sketcher::SketchObject] Sketch022
  FullyConstrained = true
  MapMode = 5
  Support = -> [XY_Plane005]
  sketch-geometry (4):
    g0: LineSegment StartX=-25 StartY=25 StartZ=0 EndX=25 EndY=25 EndZ=0
    g1: LineSegment StartX=25 StartY=25 StartZ=0 EndX=25 EndY=-25 EndZ=0
    g2: LineSegment StartX=25 StartY=-25 StartZ=0 EndX=-25 EndY=-25 EndZ=0
    g3: LineSegment StartX=-25 StartY=-25 StartZ=0 EndX=-25 EndY=25 EndZ=0
  constraints (10):
    c: Coincident(g0,g1)
    c: Coincident(g1,g2)
    c: Coincident(g2,g3)
    c: Coincident(g3,g0)
    c: Horizontal(g0)
    c: Vertical(g3)
    c: Symmetric(g2,g1,g-2)
    c: Symmetric(g1,g0,g-1)
    c: DistanceY(g1,g1) = 50
    c: DistanceX(g2,g2) = 50
FEATURE [PartDesign::Pad] Pad004
  Direction = (0,0,1)
  Length = 20
  Length2 = 10
  Profile = -> Sketch022
  ReferenceAxis = -> Sketch022 [N_Axis]
  Type = 0
FEATURE [Sketcher::SketchObject] Sketch023
  ExternalGeometry = -> [Pad004]
  FullyConstrained = true
  MapMode = 5
  Placement = pos=(0,0,20) rot=(0,0,1;0rad)
  Support = -> [Pad004]
  sketch-geometry (36):
    g0: LineSegment StartX=-18 StartY=15 StartZ=0 EndX=-17 EndY=15 EndZ=0
    g1: LineSegment StartX=20 StartY=13 StartZ=0 EndX=20 EndY=-13 EndZ=0
    g2: LineSegment StartX=18 StartY=-15 StartZ=0 EndX=17 EndY=-15 EndZ=0
    g3: LineSegment StartX=-20 StartY=-13 StartZ=0 EndX=-20 EndY=13 EndZ=0
    g4: LineSegment StartX=-13 StartY=20 StartZ=0 EndX=13 EndY=20 EndZ=0
    g5: LineSegment StartX=15 StartY=18 StartZ=0 EndX=15 EndY=17 EndZ=0
    g6: LineSegment StartX=13 StartY=-20 StartZ=0 EndX=-13 EndY=-20 EndZ=0
    g7: LineSegment StartX=-15 StartY=-18 StartZ=0 EndX=-15 EndY=-17 EndZ=0
    g8: LineSegment StartX=17 StartY=15 StartZ=0 EndX=18 EndY=15 EndZ=0
    g9: LineSegment StartX=-15 StartY=17 StartZ=0 EndX=-15 EndY=18 EndZ=0
    g10: LineSegment StartX=-17 StartY=-15 StartZ=0 EndX=-18 EndY=-15 EndZ=0
    g11: LineSegment StartX=15 StartY=-17 StartZ=0 EndX=15 EndY=-18 EndZ=0
    g12: ArcOfCircle CenterX=-13 CenterY=-18 CenterZ=0 NormalX=0 NormalY=0 NormalZ=1 AngleXU=0 Radius=2 StartAngle=3.14159 EndAngle=4.71239
    g13: GeomPoint X=-15 Y=-20 Z=0
    g14: ArcOfCircle CenterX=13 CenterY=-18 CenterZ=0 NormalX=0 NormalY=0 NormalZ=1 AngleXU=0 Radius=2 StartAngle=4.71239 EndAngle=6.28319
    g15: GeomPoint X=15 Y=-20 Z=0
    g16: ArcOfCircle CenterX=17 CenterY=-17 CenterZ=0 NormalX=0 NormalY=0 NormalZ=1 AngleXU=0 Radius=2 StartAngle=1.5708 EndAngle=3.14159
    g17: GeomPoint X=15 Y=-15 Z=0
    g18: ArcOfCircle CenterX=18 CenterY=-13 CenterZ=0 NormalX=0 NormalY=0 NormalZ=1 AngleXU=0 Radius=2 StartAngle=4.71239 EndAngle=6.28319
    g19: GeomPoint X=20 Y=-15 Z=0
    g20: ArcOfCircle CenterX=18 CenterY=13 CenterZ=0 NormalX=0 NormalY=0 NormalZ=1 AngleXU=0 Radius=2 StartAngle=0 EndAngle=1.5708
    g21: GeomPoint X=20 Y=15 Z=0
    g22: ArcOfCircle CenterX=17 CenterY=17 CenterZ=0 NormalX=0 NormalY=0 NormalZ=1 AngleXU=0 Radius=2 StartAngle=3.14159 EndAngle=4.71239
    g23: GeomPoint X=15 Y=15 Z=0
    g24: ArcOfCircle CenterX=13 CenterY=18 CenterZ=0 NormalX=0 NormalY=0 NormalZ=1 AngleXU=0 Radius=2 StartAngle=4e-16 EndAngle=1.5708
    g25: GeomPoint X=15 Y=20 Z=0
    g26: ArcOfCircle CenterX=-13 CenterY=18 CenterZ=0 NormalX=0 NormalY=0 NormalZ=1 AngleXU=0 Radius=2 StartAngle=1.5708 EndAngle=3.14159
    g27: GeomPoint X=-15 Y=20 Z=0
    g28: ArcOfCircle CenterX=-17 CenterY=17 CenterZ=0 NormalX=0 NormalY=0 NormalZ=1 AngleXU=0 Radius=2 StartAngle=4.71239 EndAngle=6.28319
    g29: GeomPoint X=-15 Y=15 Z=0
    g30: ArcOfCircle CenterX=-18 CenterY=13 CenterZ=0 NormalX=0 NormalY=0 NormalZ=1 AngleXU=0 Radius=2 StartAngle=1.5708 EndAngle=3.14159
    g31: GeomPoint X=-20 Y=15 Z=0
    g32: ArcOfCircle CenterX=-18 CenterY=-13 CenterZ=0 NormalX=0 NormalY=0 NormalZ=1 AngleXU=0 Radius=2 StartAngle=3.14159 EndAngle=4.71239
    g33: GeomPoint X=-20 Y=-15 Z=0
    g34: ArcOfCircle CenterX=-17 CenterY=-17 CenterZ=0 NormalX=0 NormalY=0 NormalZ=1 AngleXU=0 Radius=2 StartAngle=0 EndAngle=1.5708
    g35: GeomPoint X=-15 Y=-15 Z=0
  constraints (80):
    c: Horizontal(g2)
    c: Vertical(g3)
    c: Symmetric(g21,g31,g-2)
    c: Symmetric(g21,g19,g-1)
    c: DistanceX(g31,g21) = 40
    c: DistanceY(g19,g21) = 30
    c: Horizontal(g4)
    c: Vertical(g7)
    c: Symmetric(g13,g15,g-2)
    c: Symmetric(g15,g25,g-1)
    c: DistanceY(g15,g25) = 40
    c: Vertical(g9)
    c: Vertical(g5)
    c: Vertical(g11)
    c: Horizontal(g10)
    c: Horizontal(g8)
    c: Horizontal(g0)
    c: DistanceX(g13,g15) = 30
    c: DistanceY(g33,g31) = 30
    c: DistanceX(g27,g25) = 30
    c: PointOnObject(g13,g7)
    c: PointOnObject(g13,g6)
    c: Tangent(g7,g12) = 1.5708
    c: Tangent(g6,g12) = 1.5708
    c: Radius(g12) = 2
    c: PointOnObject(g15,g11)
    c: PointOnObject(g15,g6)
    c: Tangent(g11,g14) = 1.5708
    c: Tangent(g6,g14) = 1.5708
    c: PointOnObject(g17,g11)
    c: PointOnObject(g17,g2)
    c: Tangent(g11,g16) = -1.5708
    c: Tangent(g2,g16) = -1.5708
    c: PointOnObject(g19,g2)
    c: PointOnObject(g19,g1)
    c: Tangent(g2,g18) = 1.5708
    c: Tangent(g1,g18) = 1.5708
    c: PointOnObject(g21,g1)
    c: PointOnObject(g21,g8)
    c: Tangent(g1,g20) = 1.5708
    c: Tangent(g8,g20) = 1.5708
    c: PointOnObject(g23,g8)
    c: PointOnObject(g23,g5)
    c: Tangent(g8,g22) = -1.5708
    c: Tangent(g5,g22) = -1.5708
    c: PointOnObject(g25,g5)
    c: PointOnObject(g25,g4)
    c: Tangent(g5,g24) = 1.5708
    c: Tangent(g4,g24) = 1.5708
    c: PointOnObject(g27,g9)
    c: PointOnObject(g27,g4)
    c: Tangent(g9,g26) = 1.5708
    c: Tangent(g4,g26) = 1.5708
    c: PointOnObject(g29,g9)
    c: PointOnObject(g29,g0)
    c: Tangent(g9,g28) = -1.5708
    c: Tangent(g0,g28) = -1.5708
    c: PointOnObject(g31,g0)
    c: PointOnObject(g31,g3)
    c: Tangent(g0,g30) = 1.5708
    c: Tangent(g3,g30) = 1.5708
    c: PointOnObject(g33,g3)
    c: PointOnObject(g33,g10)
    c: Tangent(g3,g32) = 1.5708
    c: Tangent(g10,g32) = 1.5708
    c: PointOnObject(g35,g10)
    c: PointOnObject(g35,g7)
    c: Tangent(g10,g34) = -1.5708
    c: Tangent(g7,g34) = -1.5708
    c: Radius(g34) = 2
    c: Radius(g32) = 2
    c: Radius(g30) = 2
    c: Radius(g28) = 2
    c: Radius(g26) = 2
    c: Radius(g24) = 2
    c: Radius(g22) = 2
    c: Radius(g20) = 2
    c: Radius(g18) = 2
    c: Radius(g16) = 2
    c: Radius(g14) = 2
FEATURE [PartDesign::Pocket] Pocket019
  BaseFeature = -> Pad004
  Direction = (0,0,-1)
  Length = 5
  Length2 = 5
  Profile = -> Sketch023
  ReferenceAxis = -> Sketch023 [N_Axis]
  Type = 1
FEATURE [Sketcher::SketchObject] Sketch024
  ExternalGeometry = -> [Pocket019]
  FullyConstrained = true
  MapMode = 5
  Placement = pos=(25,0,0) rot=(0.57735,0.57735,0.57735;2.0944rad)
  Support = -> [Pocket019]
  sketch-geometry (6):
    g0: LineSegment StartX=-15 StartY=10 StartZ=0 EndX=15 EndY=10 EndZ=0
    g1: LineSegment StartX=20 StartY=5 StartZ=0 EndX=20 EndY=0 EndZ=0
    g2: LineSegment StartX=20 StartY=0 StartZ=0 EndX=-20 EndY=0 EndZ=0
    g3: LineSegment StartX=-20 StartY=0 StartZ=0 EndX=-20 EndY=5 EndZ=0
    g4: ArcOfCircle CenterX=15 CenterY=5 CenterZ=0 NormalX=0 NormalY=0 NormalZ=1 AngleXU=0 Radius=5 StartAngle=1.11001e-11 EndAngle=1.5708
    g5: ArcOfCircle CenterX=-15 CenterY=5 CenterZ=0 NormalX=0 NormalY=0 NormalZ=1 AngleXU=0 Radius=5 StartAngle=1.5708 EndAngle=3.14159
  constraints (15):
    c: Coincident(g1,g2)
    c: Coincident(g2,g3)
    c: Vertical(g1)
    c: Vertical(g3)
    c: PointOnObject(g1,g-1)
    c: Tangent(g1,g4) = 1.5708
    c: Tangent(g0,g4) = 1.5708
    c: Tangent(g0,g5) = 1.5708
    c: Tangent(g3,g5) = 1.5708
    c: Horizontal(g0)
    c: DistanceX(g2,g2) = 40
    c: Symmetric(g2,g1,g-2)
    c: Distance(g-1,g0) = 10
    c: Radius(g5) = 5
    c: Radius(g4) = 5
FEATURE [PartDesign::Pocket] Pocket020
  BaseFeature = -> Pocket019
  Direction = (-1,0,0)
  Length = 5
  Length2 = 5
  Profile = -> Sketch024
  ReferenceAxis = -> Sketch024 [N_Axis]
  Type = 1
FEATURE [Sketcher::SketchObject] Sketch025
  FullyConstrained = true
  MapMode = 5
  Placement = pos=(0,-25,0) rot=(1,0,0;1.5708rad)
  Support = -> [Pocket019]
  sketch-geometry (6):
    g0: LineSegment StartX=-15 StartY=10 StartZ=0 EndX=15 EndY=10 EndZ=0
    g1: LineSegment StartX=20 StartY=5 StartZ=0 EndX=20 EndY=0 EndZ=0
    g2: LineSegment StartX=20 StartY=0 StartZ=0 EndX=-20 EndY=0 EndZ=0
    g3: LineSegment StartX=-20 StartY=0 StartZ=0 EndX=-20 EndY=5 EndZ=0
    g4: ArcOfCircle CenterX=15 CenterY=5 CenterZ=0 NormalX=0 NormalY=0 NormalZ=1 AngleXU=0 Radius=5 StartAngle=1.11e-11 EndAngle=1.5708
    g5: ArcOfCircle CenterX=-15 CenterY=5 CenterZ=0 NormalX=0 NormalY=0 NormalZ=1 AngleXU=0 Radius=5 StartAngle=1.5708 EndAngle=3.14159
  constraints (15):
    c: Coincident(g1,g2)
    c: Coincident(g2,g3)
    c: Horizontal(g0)
    c: Vertical(g1)
    c: Vertical(g3)
    c: Symmetric(g2,g1,g-2)
    c: PointOnObject(g1,g-1)
    c: Tangent(g0,g4) = 1.5708
    c: Tangent(g1,g4) = 1.5708
    c: Tangent(g0,g5) = 1.5708
    c: Tangent(g3,g5) = 1.5708
    c: DistanceX(g2,g2) = 40
    c: Distance(g-1,g0) = 10
    c: Radius(g5) = 5
    c: Radius(g4) = 5
FEATURE [PartDesign::Pocket] Pocket021
  BaseFeature = -> Pocket020
  Direction = (0,1,-2e-16)
  Length = 5
  Length2 = 5
  Profile = -> Sketch025
  ReferenceAxis = -> Sketch025 [N_Axis]
  Type = 1
FEATURE [Sketcher::SketchObject] Sketch026
  FullyConstrained = false
  MapMode = 5
  Placement = pos=(0,0,20) rot=(0,0,1;0rad)
  sketch-geometry (4):
    g0: Circle CenterX=-20 CenterY=20 CenterZ=0 NormalX=0 NormalY=0 NormalZ=1 AngleXU=0 Radius=1.55
    g1: Circle CenterX=20 CenterY=20 CenterZ=0 NormalX=0 NormalY=0 NormalZ=1 AngleXU=0 Radius=1.55
    g2: Circle CenterX=20 CenterY=-20 CenterZ=0 NormalX=0 NormalY=0 NormalZ=1 AngleXU=0 Radius=1.55
    g3: Circle CenterX=-20 CenterY=-20 CenterZ=0 NormalX=0 NormalY=0 NormalZ=1 AngleXU=0 Radius=1.55
  constraints (4):
    c: Diameter(g0) = 3.1
    c: Diameter(g1) = 3.1
    c: Diameter(g2) = 3.1
    c: Diameter(g3) = 3.1
FEATURE [PartDesign::Pocket] Pocket022
  BaseFeature = -> Pocket021
  Direction = (0,0,-1)
  Length = 5
  Length2 = 5
  Profile = -> Sketch026
  ReferenceAxis = -> Sketch026 [N_Axis]
  Type = 0
FEATURE [Sketcher::SketchObject] Sketch027
  ExternalGeometry = -> [Pocket022]
  FullyConstrained = true
  MapMode = 5
  Placement = pos=(0,-25,0) rot=(1,0,0;1.5708rad)
  Support = -> [Pocket022]
  sketch-geometry (2):
    g0: Circle CenterX=-20 CenterY=14 CenterZ=0 NormalX=0 NormalY=0 NormalZ=1 AngleXU=0 Radius=1.4
    g1: Circle CenterX=20 CenterY=14 CenterZ=0 NormalX=0 NormalY=0 NormalZ=1 AngleXU=0 Radius=1.4
  constraints (6):
    c: Diameter(g0) = 2.8
    c: Diameter(g1) = 2.8
    c: Distance(g0,g-5) = 5
    c: Distance(g0,g-3) = 6
    c: Distance(g1,g-3) = 6
    c: Distance(g1,g-4) = 5
FEATURE [PartDesign::Pocket] Pocket023
  BaseFeature = -> Pocket022
  Direction = (0,1,-2e-16)
  Length = 3
  Length2 = 5
  Profile = -> Sketch027
  ReferenceAxis = -> Sketch027 [N_Axis]
  Type = 0
FEATURE [PartDesign::Body] Body005  label="BackplaneBlock003"
  Group = -> [Sketch022,Pad004,Sketch023,Pocket019,Sketch024,Sketch025,Pocket020,Pocket021,Sketch026,Pocket022,Sketch027,Pocket023]
  Origin = -> Origin005
  Placement = pos=(25,85,0) rot=(0,0,-1;1.5708rad)
  Tip = -> Pocket023
FEATURE [Sketcher::SketchObject] Sketch028
  FullyConstrained = true
  MapMode = 5
  Support = -> [XY_Plane006]
  sketch-geometry (4):
    g0: LineSegment StartX=-25 StartY=25 StartZ=0 EndX=25 EndY=25 EndZ=0
    g1: LineSegment StartX=25 StartY=25 StartZ=0 EndX=25 EndY=-25 EndZ=0
    g2: LineSegment StartX=25 StartY=-25 StartZ=0 EndX=-25 EndY=-25 EndZ=0
    g3: LineSegment StartX=-25 StartY=-25 StartZ=0 EndX=-25 EndY=25 EndZ=0
  constraints (10):
    c: Coincident(g0,g1)
    c: Coincident(g1,g2)
    c: Coincident(g2,g3)
    c: Coincident(g3,g0)
    c: Horizontal(g0)
    c: Vertical(g3)
    c: Symmetric(g2,g1,g-2)
    c: Symmetric(g1,g0,g-1)
    c: DistanceY(g1,g1) = 50
    c: DistanceX(g2,g2) = 50
FEATURE [PartDesign::Pad] Pad005
  Direction = (0,0,1)
  Length = 20
  Length2 = 10
  Profile = -> Sketch028
  ReferenceAxis = -> Sketch028 [N_Axis]
  Type = 0
FEATURE [Sketcher::SketchObject] Sketch029
  ExternalGeometry = -> [Pad005]
  FullyConstrained = true
  MapMode = 5
  Placement = pos=(0,0,20) rot=(0,0,1;0rad)
  Support = -> [Pad005]
  sketch-geometry (36):
    g0: LineSegment StartX=-18 StartY=15 StartZ=0 EndX=-17 EndY=15 EndZ=0
    g1: LineSegment StartX=20 StartY=13 StartZ=0 EndX=20 EndY=-13 EndZ=0
    g2: LineSegment StartX=18 StartY=-15 StartZ=0 EndX=17 EndY=-15 EndZ=0
    g3: LineSegment StartX=-20 StartY=-13 StartZ=0 EndX=-20 EndY=13 EndZ=0
    g4: LineSegment StartX=-13 StartY=20 StartZ=0 EndX=13 EndY=20 EndZ=0
    g5: LineSegment StartX=15 StartY=18 StartZ=0 EndX=15 EndY=17 EndZ=0
    g6: LineSegment StartX=13 StartY=-20 StartZ=0 EndX=-13 EndY=-20 EndZ=0
    g7: LineSegment StartX=-15 StartY=-18 StartZ=0 EndX=-15 EndY=-17 EndZ=0
    g8: LineSegment StartX=17 StartY=15 StartZ=0 EndX=18 EndY=15 EndZ=0
    g9: LineSegment StartX=-15 StartY=17 StartZ=0 EndX=-15 EndY=18 EndZ=0
    g10: LineSegment StartX=-17 StartY=-15 StartZ=0 EndX=-18 EndY=-15 EndZ=0
    g11: LineSegment StartX=15 StartY=-17 StartZ=0 EndX=15 EndY=-18 EndZ=0
    g12: ArcOfCircle CenterX=-13 CenterY=-18 CenterZ=0 NormalX=0 NormalY=0 NormalZ=1 AngleXU=0 Radius=2 StartAngle=3.14159 EndAngle=4.71239
    g13: GeomPoint X=-15 Y=-20 Z=0
    g14: ArcOfCircle CenterX=13 CenterY=-18 CenterZ=0 NormalX=0 NormalY=0 NormalZ=1 AngleXU=0 Radius=2 StartAngle=4.71239 EndAngle=6.28319
    g15: GeomPoint X=15 Y=-20 Z=0
    g16: ArcOfCircle CenterX=17 CenterY=-17 CenterZ=0 NormalX=0 NormalY=0 NormalZ=1 AngleXU=0 Radius=2 StartAngle=1.5708 EndAngle=3.14159
    g17: GeomPoint X=15 Y=-15 Z=0
    g18: ArcOfCircle CenterX=18 CenterY=-13 CenterZ=0 NormalX=0 NormalY=0 NormalZ=1 AngleXU=0 Radius=2 StartAngle=4.71239 EndAngle=6.28319
    g19: GeomPoint X=20 Y=-15 Z=0
    g20: ArcOfCircle CenterX=18 CenterY=13 CenterZ=0 NormalX=0 NormalY=0 NormalZ=1 AngleXU=0 Radius=2 StartAngle=0 EndAngle=1.5708
    g21: GeomPoint X=20 Y=15 Z=0
    g22: ArcOfCircle CenterX=17 CenterY=17 CenterZ=0 NormalX=0 NormalY=0 NormalZ=1 AngleXU=0 Radius=2 StartAngle=3.14159 EndAngle=4.71239
    g23: GeomPoint X=15 Y=15 Z=0
    g24: ArcOfCircle CenterX=13 CenterY=18 CenterZ=0 NormalX=0 NormalY=0 NormalZ=1 AngleXU=0 Radius=2 StartAngle=4e-16 EndAngle=1.5708
    g25: GeomPoint X=15 Y=20 Z=0
    g26: ArcOfCircle CenterX=-13 CenterY=18 CenterZ=0 NormalX=0 NormalY=0 NormalZ=1 AngleXU=0 Radius=2 StartAngle=1.5708 EndAngle=3.14159
    g27: GeomPoint X=-15 Y=20 Z=0
    g28: ArcOfCircle CenterX=-17 CenterY=17 CenterZ=0 NormalX=0 NormalY=0 NormalZ=1 AngleXU=0 Radius=2 StartAngle=4.71239 EndAngle=6.28319
    g29: GeomPoint X=-15 Y=15 Z=0
    g30: ArcOfCircle CenterX=-18 CenterY=13 CenterZ=0 NormalX=0 NormalY=0 NormalZ=1 AngleXU=0 Radius=2 StartAngle=1.5708 EndAngle=3.14159
    g31: GeomPoint X=-20 Y=15 Z=0
    g32: ArcOfCircle CenterX=-18 CenterY=-13 CenterZ=0 NormalX=0 NormalY=0 NormalZ=1 AngleXU=0 Radius=2 StartAngle=3.14159 EndAngle=4.71239
    g33: GeomPoint X=-20 Y=-15 Z=0
    g34: ArcOfCircle CenterX=-17 CenterY=-17 CenterZ=0 NormalX=0 NormalY=0 NormalZ=1 AngleXU=0 Radius=2 StartAngle=0 EndAngle=1.5708
    g35: GeomPoint X=-15 Y=-15 Z=0
  constraints (80):
    c: Horizontal(g2)
    c: Vertical(g3)
    c: Symmetric(g21,g31,g-2)
    c: Symmetric(g21,g19,g-1)
    c: DistanceX(g31,g21) = 40
    c: DistanceY(g19,g21) = 30
    c: Horizontal(g4)
    c: Vertical(g7)
    c: Symmetric(g13,g15,g-2)
    c: Symmetric(g15,g25,g-1)
    c: DistanceY(g15,g25) = 40
    c: Vertical(g9)
    c: Vertical(g5)
    c: Vertical(g11)
    c: Horizontal(g10)
    c: Horizontal(g8)
    c: Horizontal(g0)
    c: DistanceX(g13,g15) = 30
    c: DistanceY(g33,g31) = 30
    c: DistanceX(g27,g25) = 30
    c: PointOnObject(g13,g7)
    c: PointOnObject(g13,g6)
    c: Tangent(g7,g12) = 1.5708
    c: Tangent(g6,g12) = 1.5708
    c: Radius(g12) = 2
    c: PointOnObject(g15,g11)
    c: PointOnObject(g15,g6)
    c: Tangent(g11,g14) = 1.5708
    c: Tangent(g6,g14) = 1.5708
    c: PointOnObject(g17,g11)
    c: PointOnObject(g17,g2)
    c: Tangent(g11,g16) = -1.5708
    c: Tangent(g2,g16) = -1.5708
    c: PointOnObject(g19,g2)
    c: PointOnObject(g19,g1)
    c: Tangent(g2,g18) = 1.5708
    c: Tangent(g1,g18) = 1.5708
    c: PointOnObject(g21,g1)
    c: PointOnObject(g21,g8)
    c: Tangent(g1,g20) = 1.5708
    c: Tangent(g8,g20) = 1.5708
    c: PointOnObject(g23,g8)
    c: PointOnObject(g23,g5)
    c: Tangent(g8,g22) = -1.5708
    c: Tangent(g5,g22) = -1.5708
    c: PointOnObject(g25,g5)
    c: PointOnObject(g25,g4)
    c: Tangent(g5,g24) = 1.5708
    c: Tangent(g4,g24) = 1.5708
    c: PointOnObject(g27,g9)
    c: PointOnObject(g27,g4)
    c: Tangent(g9,g26) = 1.5708
    c: Tangent(g4,g26) = 1.5708
    c: PointOnObject(g29,g9)
    c: PointOnObject(g29,g0)
    c: Tangent(g9,g28) = -1.5708
    c: Tangent(g0,g28) = -1.5708
    c: PointOnObject(g31,g0)
    c: PointOnObject(g31,g3)
    c: Tangent(g0,g30) = 1.5708
    c: Tangent(g3,g30) = 1.5708
    c: PointOnObject(g33,g3)
    c: PointOnObject(g33,g10)
    c: Tangent(g3,g32) = 1.5708
    c: Tangent(g10,g32) = 1.5708
    c: PointOnObject(g35,g10)
    c: PointOnObject(g35,g7)
    c: Tangent(g10,g34) = -1.5708
    c: Tangent(g7,g34) = -1.5708
    c: Radius(g34) = 2
    c: Radius(g32) = 2
    c: Radius(g30) = 2
    c: Radius(g28) = 2
    c: Radius(g26) = 2
    c: Radius(g24) = 2
    c: Radius(g22) = 2
    c: Radius(g20) = 2
    c: Radius(g18) = 2
    c: Radius(g16) = 2
    c: Radius(g14) = 2
FEATURE [PartDesign::Pocket] Pocket024
  BaseFeature = -> Pad005
  Direction = (0,0,-1)
  Length = 5
  Length2 = 5
  Profile = -> Sketch029
  ReferenceAxis = -> Sketch029 [N_Axis]
  Type = 1
FEATURE [Sketcher::SketchObject] Sketch030
  ExternalGeometry = -> [Pocket024]
  FullyConstrained = true
  MapMode = 5
  Placement = pos=(25,0,0) rot=(0.57735,0.57735,0.57735;2.0944rad)
  Support = -> [Pocket024]
  sketch-geometry (6):
    g0: LineSegment StartX=-15 StartY=10 StartZ=0 EndX=15 EndY=10 EndZ=0
    g1: LineSegment StartX=20 StartY=5 StartZ=0 EndX=20 EndY=0 EndZ=0
    g2: LineSegment StartX=20 StartY=0 StartZ=0 EndX=-20 EndY=0 EndZ=0
    g3: LineSegment StartX=-20 StartY=0 StartZ=0 EndX=-20 EndY=5 EndZ=0
    g4: ArcOfCircle CenterX=15 CenterY=5 CenterZ=0 NormalX=0 NormalY=0 NormalZ=1 AngleXU=0 Radius=5 StartAngle=1.11001e-11 EndAngle=1.5708
    g5: ArcOfCircle CenterX=-15 CenterY=5 CenterZ=0 NormalX=0 NormalY=0 NormalZ=1 AngleXU=0 Radius=5 StartAngle=1.5708 EndAngle=3.14159
  constraints (15):
    c: Coincident(g1,g2)
    c: Coincident(g2,g3)
    c: Vertical(g1)
    c: Vertical(g3)
    c: PointOnObject(g1,g-1)
    c: Tangent(g1,g4) = 1.5708
    c: Tangent(g0,g4) = 1.5708
    c: Tangent(g0,g5) = 1.5708
    c: Tangent(g3,g5) = 1.5708
    c: Horizontal(g0)
    c: DistanceX(g2,g2) = 40
    c: Symmetric(g2,g1,g-2)
    c: Distance(g-1,g0) = 10
    c: Radius(g5) = 5
    c: Radius(g4) = 5
FEATURE [PartDesign::Pocket] Pocket025
  BaseFeature = -> Pocket024
  Direction = (-1,0,0)
  Length = 5
  Length2 = 5
  Profile = -> Sketch030
  ReferenceAxis = -> Sketch030 [N_Axis]
  Type = 1
FEATURE [Sketcher::SketchObject] Sketch031
  FullyConstrained = true
  MapMode = 5
  Placement = pos=(0,-25,0) rot=(1,0,0;1.5708rad)
  Support = -> [Pocket024]
  sketch-geometry (6):
    g0: LineSegment StartX=-15 StartY=10 StartZ=0 EndX=15 EndY=10 EndZ=0
    g1: LineSegment StartX=20 StartY=5 StartZ=0 EndX=20 EndY=0 EndZ=0
    g2: LineSegment StartX=20 StartY=0 StartZ=0 EndX=-20 EndY=0 EndZ=0
    g3: LineSegment StartX=-20 StartY=0 StartZ=0 EndX=-20 EndY=5 EndZ=0
    g4: ArcOfCircle CenterX=15 CenterY=5 CenterZ=0 NormalX=0 NormalY=0 NormalZ=1 AngleXU=0 Radius=5 StartAngle=1.11e-11 EndAngle=1.5708
    g5: ArcOfCircle CenterX=-15 CenterY=5 CenterZ=0 NormalX=0 NormalY=0 NormalZ=1 AngleXU=0 Radius=5 StartAngle=1.5708 EndAngle=3.14159
  constraints (15):
    c: Coincident(g1,g2)
    c: Coincident(g2,g3)
    c: Horizontal(g0)
    c: Vertical(g1)
    c: Vertical(g3)
    c: Symmetric(g2,g1,g-2)
    c: PointOnObject(g1,g-1)
    c: Tangent(g0,g4) = 1.5708
    c: Tangent(g1,g4) = 1.5708
    c: Tangent(g0,g5) = 1.5708
    c: Tangent(g3,g5) = 1.5708
    c: DistanceX(g2,g2) = 40
    c: Distance(g-1,g0) = 10
    c: Radius(g5) = 5
    c: Radius(g4) = 5
FEATURE [PartDesign::Pocket] Pocket026
  BaseFeature = -> Pocket025
  Direction = (0,1,-2e-16)
  Length = 5
  Length2 = 5
  Profile = -> Sketch031
  ReferenceAxis = -> Sketch031 [N_Axis]
  Type = 1
FEATURE [Sketcher::SketchObject] Sketch032
  FullyConstrained = false
  MapMode = 5
  Placement = pos=(0,0,20) rot=(0,0,1;0rad)
  sketch-geometry (4):
    g0: Circle CenterX=-20 CenterY=20 CenterZ=0 NormalX=0 NormalY=0 NormalZ=1 AngleXU=0 Radius=1.55
    g1: Circle CenterX=20 CenterY=20 CenterZ=0 NormalX=0 NormalY=0 NormalZ=1 AngleXU=0 Radius=1.55
    g2: Circle CenterX=20 CenterY=-20 CenterZ=0 NormalX=0 NormalY=0 NormalZ=1 AngleXU=0 Radius=1.55
    g3: Circle CenterX=-20 CenterY=-20 CenterZ=0 NormalX=0 NormalY=0 NormalZ=1 AngleXU=0 Radius=1.55
  constraints (4):
    c: Diameter(g0) = 3.1
    c: Diameter(g1) = 3.1
    c: Diameter(g2) = 3.1
    c: Diameter(g3) = 3.1
FEATURE [PartDesign::Pocket] Pocket027
  BaseFeature = -> Pocket026
  Direction = (0,0,-1)
  Length = 5
  Length2 = 5
  Profile = -> Sketch032
  ReferenceAxis = -> Sketch032 [N_Axis]
  Type = 0
FEATURE [Sketcher::SketchObject] Sketch033
  ExternalGeometry = -> [Pocket027]
  FullyConstrained = true
  MapMode = 5
  Placement = pos=(0,-25,0) rot=(1,0,0;1.5708rad)
  Support = -> [Pocket027]
  sketch-geometry (2):
    g0: Circle CenterX=-20 CenterY=14 CenterZ=0 NormalX=0 NormalY=0 NormalZ=1 AngleXU=0 Radius=1.4
    g1: Circle CenterX=20 CenterY=14 CenterZ=0 NormalX=0 NormalY=0 NormalZ=1 AngleXU=0 Radius=1.4
  constraints (6):
    c: Diameter(g0) = 2.8
    c: Diameter(g1) = 2.8
    c: Distance(g0,g-5) = 5
    c: Distance(g0,g-3) = 6
    c: Distance(g1,g-3) = 6
    c: Distance(g1,g-4) = 5
FEATURE [PartDesign::Pocket] Pocket028
  BaseFeature = -> Pocket027
  Direction = (0,1,-2e-16)
  Length = 3
  Length2 = 5
  Profile = -> Sketch033
  ReferenceAxis = -> Sketch033 [N_Axis]
  Type = 0
FEATURE [PartDesign::Body] Body006  label="BackplaneBlock004"
  Group = -> [Sketch028,Pad005,Sketch029,Pocket024,Sketch030,Sketch031,Pocket025,Pocket026,Sketch032,Pocket027,Sketch033,Pocket028]
  Origin = -> Origin006
  Placement = pos=(145,85,0) rot=(0,0,1;1.5708rad)
  Tip = -> Pocket028
FEATURE [Sketcher::SketchObject] Sketch034
  FullyConstrained = true
  MapMode = 5
  Support = -> [XY_Plane007]
  sketch-geometry (4):
    g0: LineSegment StartX=-25 StartY=25 StartZ=0 EndX=25 EndY=25 EndZ=0
    g1: LineSegment StartX=25 StartY=25 StartZ=0 EndX=25 EndY=-25 EndZ=0
    g2: LineSegment StartX=25 StartY=-25 StartZ=0 EndX=-25 EndY=-25 EndZ=0
    g3: LineSegment StartX=-25 StartY=-25 StartZ=0 EndX=-25 EndY=25 EndZ=0
  constraints (10):
    c: Coincident(g0,g1)
    c: Coincident(g1,g2)
    c: Coincident(g2,g3)
    c: Coincident(g3,g0)
    c: Horizontal(g0)
    c: Vertical(g3)
    c: Symmetric(g2,g1,g-2)
    c: Symmetric(g1,g0,g-1)
    c: DistanceY(g1,g1) = 50
    c: DistanceX(g2,g2) = 50
FEATURE [PartDesign::Pad] Pad006
  Direction = (0,0,1)
  Length = 20
  Length2 = 10
  Profile = -> Sketch034
  ReferenceAxis = -> Sketch034 [N_Axis]
  Type = 0
FEATURE [Sketcher::SketchObject] Sketch035
  ExternalGeometry = -> [Pad006]
  FullyConstrained = true
  MapMode = 5
  Placement = pos=(0,0,20) rot=(0,0,1;0rad)
  Support = -> [Pad006]
  sketch-geometry (36):
    g0: LineSegment StartX=-18 StartY=15 StartZ=0 EndX=-17 EndY=15 EndZ=0
    g1: LineSegment StartX=20 StartY=13 StartZ=0 EndX=20 EndY=-13 EndZ=0
    g2: LineSegment StartX=18 StartY=-15 StartZ=0 EndX=17 EndY=-15 EndZ=0
    g3: LineSegment StartX=-20 StartY=-13 StartZ=0 EndX=-20 EndY=13 EndZ=0
    g4: LineSegment StartX=-13 StartY=20 StartZ=0 EndX=13 EndY=20 EndZ=0
    g5: LineSegment StartX=15 StartY=18 StartZ=0 EndX=15 EndY=17 EndZ=0
    g6: LineSegment StartX=13 StartY=-20 StartZ=0 EndX=-13 EndY=-20 EndZ=0
    g7: LineSegment StartX=-15 StartY=-18 StartZ=0 EndX=-15 EndY=-17 EndZ=0
    g8: LineSegment StartX=17 StartY=15 StartZ=0 EndX=18 EndY=15 EndZ=0
    g9: LineSegment StartX=-15 StartY=17 StartZ=0 EndX=-15 EndY=18 EndZ=0
    g10: LineSegment StartX=-17 StartY=-15 StartZ=0 EndX=-18 EndY=-15 EndZ=0
    g11: LineSegment StartX=15 StartY=-17 StartZ=0 EndX=15 EndY=-18 EndZ=0
    g12: ArcOfCircle CenterX=-13 CenterY=-18 CenterZ=0 NormalX=0 NormalY=0 NormalZ=1 AngleXU=0 Radius=2 StartAngle=3.14159 EndAngle=4.71239
    g13: GeomPoint X=-15 Y=-20 Z=0
    g14: ArcOfCircle CenterX=13 CenterY=-18 CenterZ=0 NormalX=0 NormalY=0 NormalZ=1 AngleXU=0 Radius=2 StartAngle=4.71239 EndAngle=6.28319
    g15: GeomPoint X=15 Y=-20 Z=0
    g16: ArcOfCircle CenterX=17 CenterY=-17 CenterZ=0 NormalX=0 NormalY=0 NormalZ=1 AngleXU=0 Radius=2 StartAngle=1.5708 EndAngle=3.14159
    g17: GeomPoint X=15 Y=-15 Z=0
    g18: ArcOfCircle CenterX=18 CenterY=-13 CenterZ=0 NormalX=0 NormalY=0 NormalZ=1 AngleXU=0 Radius=2 StartAngle=4.71239 EndAngle=6.28319
    g19: GeomPoint X=20 Y=-15 Z=0
    g20: ArcOfCircle CenterX=18 CenterY=13 CenterZ=0 NormalX=0 NormalY=0 NormalZ=1 AngleXU=0 Radius=2 StartAngle=0 EndAngle=1.5708
    g21: GeomPoint X=20 Y=15 Z=0
    g22: ArcOfCircle CenterX=17 CenterY=17 CenterZ=0 NormalX=0 NormalY=0 NormalZ=1 AngleXU=0 Radius=2 StartAngle=3.14159 EndAngle=4.71239
    g23: GeomPoint X=15 Y=15 Z=0
    g24: ArcOfCircle CenterX=13 CenterY=18 CenterZ=0 NormalX=0 NormalY=0 NormalZ=1 AngleXU=0 Radius=2 StartAngle=4e-16 EndAngle=1.5708
    g25: GeomPoint X=15 Y=20 Z=0
    g26: ArcOfCircle CenterX=-13 CenterY=18 CenterZ=0 NormalX=0 NormalY=0 NormalZ=1 AngleXU=0 Radius=2 StartAngle=1.5708 EndAngle=3.14159
    g27: GeomPoint X=-15 Y=20 Z=0
    g28: ArcOfCircle CenterX=-17 CenterY=17 CenterZ=0 NormalX=0 NormalY=0 NormalZ=1 AngleXU=0 Radius=2 StartAngle=4.71239 EndAngle=6.28319
    g29: GeomPoint X=-15 Y=15 Z=0
    g30: ArcOfCircle CenterX=-18 CenterY=13 CenterZ=0 NormalX=0 NormalY=0 NormalZ=1 AngleXU=0 Radius=2 StartAngle=1.5708 EndAngle=3.14159
    g31: GeomPoint X=-20 Y=15 Z=0
    g32: ArcOfCircle CenterX=-18 CenterY=-13 CenterZ=0 NormalX=0 NormalY=0 NormalZ=1 AngleXU=0 Radius=2 StartAngle=3.14159 EndAngle=4.71239
    g33: GeomPoint X=-20 Y=-15 Z=0
    g34: ArcOfCircle CenterX=-17 CenterY=-17 CenterZ=0 NormalX=0 NormalY=0 NormalZ=1 AngleXU=0 Radius=2 StartAngle=0 EndAngle=1.5708
    g35: GeomPoint X=-15 Y=-15 Z=0
  constraints (80):
    c: Horizontal(g2)
    c: Vertical(g3)
    c: Symmetric(g21,g31,g-2)
    c: Symmetric(g21,g19,g-1)
    c: DistanceX(g31,g21) = 40
    c: DistanceY(g19,g21) = 30
    c: Horizontal(g4)
    c: Vertical(g7)
    c: Symmetric(g13,g15,g-2)
    c: Symmetric(g15,g25,g-1)
    c: DistanceY(g15,g25) = 40
    c: Vertical(g9)
    c: Vertical(g5)
    c: Vertical(g11)
    c: Horizontal(g10)
    c: Horizontal(g8)
    c: Horizontal(g0)
    c: DistanceX(g13,g15) = 30
    c: DistanceY(g33,g31) = 30
    c: DistanceX(g27,g25) = 30
    c: PointOnObject(g13,g7)
    c: PointOnObject(g13,g6)
    c: Tangent(g7,g12) = 1.5708
    c: Tangent(g6,g12) = 1.5708
    c: Radius(g12) = 2
    c: PointOnObject(g15,g11)
    c: PointOnObject(g15,g6)
    c: Tangent(g11,g14) = 1.5708
    c: Tangent(g6,g14) = 1.5708
    c: PointOnObject(g17,g11)
    c: PointOnObject(g17,g2)
    c: Tangent(g11,g16) = -1.5708
    c: Tangent(g2,g16) = -1.5708
    c: PointOnObject(g19,g2)
    c: PointOnObject(g19,g1)
    c: Tangent(g2,g18) = 1.5708
    c: Tangent(g1,g18) = 1.5708
    c: PointOnObject(g21,g1)
    c: PointOnObject(g21,g8)
    c: Tangent(g1,g20) = 1.5708
    c: Tangent(g8,g20) = 1.5708
    c: PointOnObject(g23,g8)
    c: PointOnObject(g23,g5)
    c: Tangent(g8,g22) = -1.5708
    c: Tangent(g5,g22) = -1.5708
    c: PointOnObject(g25,g5)
    c: PointOnObject(g25,g4)
    c: Tangent(g5,g24) = 1.5708
    c: Tangent(g4,g24) = 1.5708
    c: PointOnObject(g27,g9)
    c: PointOnObject(g27,g4)
    c: Tangent(g9,g26) = 1.5708
    c: Tangent(g4,g26) = 1.5708
    c: PointOnObject(g29,g9)
    c: PointOnObject(g29,g0)
    c: Tangent(g9,g28) = -1.5708
    c: Tangent(g0,g28) = -1.5708
    c: PointOnObject(g31,g0)
    c: PointOnObject(g31,g3)
    c: Tangent(g0,g30) = 1.5708
    c: Tangent(g3,g30) = 1.5708
    c: PointOnObject(g33,g3)
    c: PointOnObject(g33,g10)
    c: Tangent(g3,g32) = 1.5708
    c: Tangent(g10,g32) = 1.5708
    c: PointOnObject(g35,g10)
    c: PointOnObject(g35,g7)
    c: Tangent(g10,g34) = -1.5708
    c: Tangent(g7,g34) = -1.5708
    c: Radius(g34) = 2
    c: Radius(g32) = 2
    c: Radius(g30) = 2
    c: Radius(g28) = 2
    c: Radius(g26) = 2
    c: Radius(g24) = 2
    c: Radius(g22) = 2
    c: Radius(g20) = 2
    c: Radius(g18) = 2
    c: Radius(g16) = 2
    c: Radius(g14) = 2
FEATURE [PartDesign::Pocket] Pocket029
  BaseFeature = -> Pad006
  Direction = (0,0,-1)
  Length = 5
  Length2 = 5
  Profile = -> Sketch035
  ReferenceAxis = -> Sketch035 [N_Axis]
  Type = 1
FEATURE [Sketcher::SketchObject] Sketch036
  ExternalGeometry = -> [Pocket029]
  FullyConstrained = true
  MapMode = 5
  Placement = pos=(25,0,0) rot=(0.57735,0.57735,0.57735;2.0944rad)
  Support = -> [Pocket029]
  sketch-geometry (6):
    g0: LineSegment StartX=-15 StartY=10 StartZ=0 EndX=15 EndY=10 EndZ=0
    g1: LineSegment StartX=20 StartY=5 StartZ=0 EndX=20 EndY=0 EndZ=0
    g2: LineSegment StartX=20 StartY=0 StartZ=0 EndX=-20 EndY=0 EndZ=0
    g3: LineSegment StartX=-20 StartY=0 StartZ=0 EndX=-20 EndY=5 EndZ=0
    g4: ArcOfCircle CenterX=15 CenterY=5 CenterZ=0 NormalX=0 NormalY=0 NormalZ=1 AngleXU=0 Radius=5 StartAngle=1.11001e-11 EndAngle=1.5708
    g5: ArcOfCircle CenterX=-15 CenterY=5 CenterZ=0 NormalX=0 NormalY=0 NormalZ=1 AngleXU=0 Radius=5 StartAngle=1.5708 EndAngle=3.14159
  constraints (15):
    c: Coincident(g1,g2)
    c: Coincident(g2,g3)
    c: Vertical(g1)
    c: Vertical(g3)
    c: PointOnObject(g1,g-1)
    c: Tangent(g1,g4) = 1.5708
    c: Tangent(g0,g4) = 1.5708
    c: Tangent(g0,g5) = 1.5708
    c: Tangent(g3,g5) = 1.5708
    c: Horizontal(g0)
    c: DistanceX(g2,g2) = 40
    c: Symmetric(g2,g1,g-2)
    c: Distance(g-1,g0) = 10
    c: Radius(g5) = 5
    c: Radius(g4) = 5
FEATURE [PartDesign::Pocket] Pocket030
  BaseFeature = -> Pocket029
  Direction = (-1,0,0)
  Length = 5
  Length2 = 5
  Profile = -> Sketch036
  ReferenceAxis = -> Sketch036 [N_Axis]
  Type = 1
FEATURE [Sketcher::SketchObject] Sketch037
  FullyConstrained = true
  MapMode = 5
  Placement = pos=(0,-25,0) rot=(1,0,0;1.5708rad)
  Support = -> [Pocket029]
  sketch-geometry (6):
    g0: LineSegment StartX=-15 StartY=10 StartZ=0 EndX=15 EndY=10 EndZ=0
    g1: LineSegment StartX=20 StartY=5 StartZ=0 EndX=20 EndY=0 EndZ=0
    g2: LineSegment StartX=20 StartY=0 StartZ=0 EndX=-20 EndY=0 EndZ=0
    g3: LineSegment StartX=-20 StartY=0 StartZ=0 EndX=-20 EndY=5 EndZ=0
    g4: ArcOfCircle CenterX=15 CenterY=5 CenterZ=0 NormalX=0 NormalY=0 NormalZ=1 AngleXU=0 Radius=5 StartAngle=1.11e-11 EndAngle=1.5708
    g5: ArcOfCircle CenterX=-15 CenterY=5 CenterZ=0 NormalX=0 NormalY=0 NormalZ=1 AngleXU=0 Radius=5 StartAngle=1.5708 EndAngle=3.14159
  constraints (15):
    c: Coincident(g1,g2)
    c: Coincident(g2,g3)
    c: Horizontal(g0)
    c: Vertical(g1)
    c: Vertical(g3)
    c: Symmetric(g2,g1,g-2)
    c: PointOnObject(g1,g-1)
    c: Tangent(g0,g4) = 1.5708
    c: Tangent(g1,g4) = 1.5708
    c: Tangent(g0,g5) = 1.5708
    c: Tangent(g3,g5) = 1.5708
    c: DistanceX(g2,g2) = 40
    c: Distance(g-1,g0) = 10
    c: Radius(g5) = 5
    c: Radius(g4) = 5
FEATURE [PartDesign::Pocket] Pocket031
  BaseFeature = -> Pocket030
  Direction = (0,1,-2e-16)
  Length = 5
  Length2 = 5
  Profile = -> Sketch037
  ReferenceAxis = -> Sketch037 [N_Axis]
  Type = 1
FEATURE [Sketcher::SketchObject] Sketch038
  FullyConstrained = false
  MapMode = 5
  Placement = pos=(0,0,20) rot=(0,0,1;0rad)
  sketch-geometry (4):
    g0: Circle CenterX=-20 CenterY=20 CenterZ=0 NormalX=0 NormalY=0 NormalZ=1 AngleXU=0 Radius=1.55
    g1: Circle CenterX=20 CenterY=20 CenterZ=0 NormalX=0 NormalY=0 NormalZ=1 AngleXU=0 Radius=1.55
    g2: Circle CenterX=20 CenterY=-20 CenterZ=0 NormalX=0 NormalY=0 NormalZ=1 AngleXU=0 Radius=1.55
    g3: Circle CenterX=-20 CenterY=-20 CenterZ=0 NormalX=0 NormalY=0 NormalZ=1 AngleXU=0 Radius=1.55
  constraints (4):
    c: Diameter(g0) = 3.1
    c: Diameter(g1) = 3.1
    c: Diameter(g2) = 3.1
    c: Diameter(g3) = 3.1
FEATURE [PartDesign::Pocket] Pocket032
  BaseFeature = -> Pocket031
  Direction = (0,0,-1)
  Length = 5
  Length2 = 5
  Profile = -> Sketch038
  ReferenceAxis = -> Sketch038 [N_Axis]
  Type = 0
FEATURE [Sketcher::SketchObject] Sketch039
  ExternalGeometry = -> [Pocket032]
  FullyConstrained = true
  MapMode = 5
  Placement = pos=(0,-25,0) rot=(1,0,0;1.5708rad)
  Support = -> [Pocket032]
  sketch-geometry (2):
    g0: Circle CenterX=-20 CenterY=14 CenterZ=0 NormalX=0 NormalY=0 NormalZ=1 AngleXU=0 Radius=1.4
    g1: Circle CenterX=20 CenterY=14 CenterZ=0 NormalX=0 NormalY=0 NormalZ=1 AngleXU=0 Radius=1.4
  constraints (6):
    c: Diameter(g0) = 2.8
    c: Diameter(g1) = 2.8
    c: Distance(g0,g-5) = 5
    c: Distance(g0,g-3) = 6
    c: Distance(g1,g-3) = 6
    c: Distance(g1,g-4) = 5
FEATURE [PartDesign::Pocket] Pocket033
  BaseFeature = -> Pocket032
  Direction = (0,1,-2e-16)
  Length = 3
  Length2 = 5
  Profile = -> Sketch039
  ReferenceAxis = -> Sketch039 [N_Axis]
  Type = 0
FEATURE [PartDesign::Body] Body007  label="BackplaneBlock005"
  Group = -> [Sketch034,Pad006,Sketch035,Pocket029,Sketch036,Sketch037,Pocket030,Pocket031,Sketch038,Pocket032,Sketch039,Pocket033]
  Origin = -> Origin007
  Placement = pos=(85,25,0) rot=(0,0,1;0rad)
  Tip = -> Pocket033
FEATURE [Sketcher::SketchObject] Sketch040
  ExternalGeometry = -> [Pocket013]
  FullyConstrained = true
  MapMode = 5
  Placement = pos=(-25,0,0) rot=(0.57735,-0.57735,-0.57735;2.0944rad)
  Support = -> [Pocket013]
  sketch-geometry (2):
    g0: Circle CenterX=-20 CenterY=14 CenterZ=0 NormalX=0 NormalY=0 NormalZ=1 AngleXU=0 Radius=1.4
    g1: Circle CenterX=20 CenterY=14 CenterZ=0 NormalX=0 NormalY=0 NormalZ=1 AngleXU=0 Radius=1.4
  constraints (6):
    c: Diameter(g0) = 2.8
    c: Diameter(g1) = 2.8
    c: Distance(g0,g-3) = 5
    c: Distance(g0,g-4) = 6
    c: Distance(g1,g-4) = 6
    c: Distance(g1,g-5) = 5
FEATURE [PartDesign::Pocket] Pocket034
  BaseFeature = -> Pocket013
  Direction = (1,0,0)
  Length = 3
  Length2 = 5
  Profile = -> Sketch040
  ReferenceAxis = -> Sketch040 [N_Axis]
  Type = 0
FEATURE [PartDesign::Body] Body002  label="BackplaneBlock"
  Group = -> [Sketch002,Pad001,Sketch003,Pocket001,Sketch004,Sketch005,Pocket002,Pocket003,Sketch009,Pocket008,Sketch015,Pocket013,Sketch040,Pocket034]
  Origin = -> Origin002
  Placement = pos=(25,25,0) rot=(0,0,1;0rad)
  Tip = -> Pocket034
FEATURE [Sketcher::SketchObject] Sketch041
  FullyConstrained = true
  MapMode = 5
  Support = -> [XY_Plane008]
  sketch-geometry (4):
    g0: LineSegment StartX=-25 StartY=25 StartZ=0 EndX=25 EndY=25 EndZ=0
    g1: LineSegment StartX=25 StartY=25 StartZ=0 EndX=25 EndY=-25 EndZ=0
    g2: LineSegment StartX=25 StartY=-25 StartZ=0 EndX=-25 EndY=-25 EndZ=0
    g3: LineSegment StartX=-25 StartY=-25 StartZ=0 EndX=-25 EndY=25 EndZ=0
  constraints (10):
    c: Coincident(g0,g1)
    c: Coincident(g1,g2)
    c: Coincident(g2,g3)
    c: Coincident(g3,g0)
    c: Horizontal(g0)
    c: Vertical(g3)
    c: Symmetric(g2,g1,g-2)
    c: Symmetric(g1,g0,g-1)
    c: DistanceY(g1,g1) = 50
    c: DistanceX(g2,g2) = 50
FEATURE [PartDesign::Pad] Pad007
  Direction = (0,0,1)
  Length = 20
  Length2 = 10
  Profile = -> Sketch041
  ReferenceAxis = -> Sketch041 [N_Axis]
  Type = 0
FEATURE [Sketcher::SketchObject] Sketch042
  ExternalGeometry = -> [Pad007]
  FullyConstrained = true
  MapMode = 5
  Placement = pos=(0,0,20) rot=(0,0,1;0rad)
  Support = -> [Pad007]
  sketch-geometry (36):
    g0: LineSegment StartX=-18 StartY=15 StartZ=0 EndX=-17 EndY=15 EndZ=0
    g1: LineSegment StartX=20 StartY=13 StartZ=0 EndX=20 EndY=-13 EndZ=0
    g2: LineSegment StartX=18 StartY=-15 StartZ=0 EndX=17 EndY=-15 EndZ=0
    g3: LineSegment StartX=-20 StartY=-13 StartZ=0 EndX=-20 EndY=13 EndZ=0
    g4: LineSegment StartX=-13 StartY=20 StartZ=0 EndX=13 EndY=20 EndZ=0
    g5: LineSegment StartX=15 StartY=18 StartZ=0 EndX=15 EndY=17 EndZ=0
    g6: LineSegment StartX=13 StartY=-20 StartZ=0 EndX=-13 EndY=-20 EndZ=0
    g7: LineSegment StartX=-15 StartY=-18 StartZ=0 EndX=-15 EndY=-17 EndZ=0
    g8: LineSegment StartX=17 StartY=15 StartZ=0 EndX=18 EndY=15 EndZ=0
    g9: LineSegment StartX=-15 StartY=17 StartZ=0 EndX=-15 EndY=18 EndZ=0
    g10: LineSegment StartX=-17 StartY=-15 StartZ=0 EndX=-18 EndY=-15 EndZ=0
    g11: LineSegment StartX=15 StartY=-17 StartZ=0 EndX=15 EndY=-18 EndZ=0
    g12: ArcOfCircle CenterX=-13 CenterY=-18 CenterZ=0 NormalX=0 NormalY=0 NormalZ=1 AngleXU=0 Radius=2 StartAngle=3.14159 EndAngle=4.71239
    g13: GeomPoint X=-15 Y=-20 Z=0
    g14: ArcOfCircle CenterX=13 CenterY=-18 CenterZ=0 NormalX=0 NormalY=0 NormalZ=1 AngleXU=0 Radius=2 StartAngle=4.71239 EndAngle=6.28319
    g15: GeomPoint X=15 Y=-20 Z=0
    g16: ArcOfCircle CenterX=17 CenterY=-17 CenterZ=0 NormalX=0 NormalY=0 NormalZ=1 AngleXU=0 Radius=2 StartAngle=1.5708 EndAngle=3.14159
    g17: GeomPoint X=15 Y=-15 Z=0
    g18: ArcOfCircle CenterX=18 CenterY=-13 CenterZ=0 NormalX=0 NormalY=0 NormalZ=1 AngleXU=0 Radius=2 StartAngle=4.71239 EndAngle=6.28319
    g19: GeomPoint X=20 Y=-15 Z=0
    g20: ArcOfCircle CenterX=18 CenterY=13 CenterZ=0 NormalX=0 NormalY=0 NormalZ=1 AngleXU=0 Radius=2 StartAngle=0 EndAngle=1.5708
    g21: GeomPoint X=20 Y=15 Z=0
    g22: ArcOfCircle CenterX=17 CenterY=17 CenterZ=0 NormalX=0 NormalY=0 NormalZ=1 AngleXU=0 Radius=2 StartAngle=3.14159 EndAngle=4.71239
    g23: GeomPoint X=15 Y=15 Z=0
    g24: ArcOfCircle CenterX=13 CenterY=18 CenterZ=0 NormalX=0 NormalY=0 NormalZ=1 AngleXU=0 Radius=2 StartAngle=4e-16 EndAngle=1.5708
    g25: GeomPoint X=15 Y=20 Z=0
    g26: ArcOfCircle CenterX=-13 CenterY=18 CenterZ=0 NormalX=0 NormalY=0 NormalZ=1 AngleXU=0 Radius=2 StartAngle=1.5708 EndAngle=3.14159
    g27: GeomPoint X=-15 Y=20 Z=0
    g28: ArcOfCircle CenterX=-17 CenterY=17 CenterZ=0 NormalX=0 NormalY=0 NormalZ=1 AngleXU=0 Radius=2 StartAngle=4.71239 EndAngle=6.28319
    g29: GeomPoint X=-15 Y=15 Z=0
    g30: ArcOfCircle CenterX=-18 CenterY=13 CenterZ=0 NormalX=0 NormalY=0 NormalZ=1 AngleXU=0 Radius=2 StartAngle=1.5708 EndAngle=3.14159
    g31: GeomPoint X=-20 Y=15 Z=0
    g32: ArcOfCircle CenterX=-18 CenterY=-13 CenterZ=0 NormalX=0 NormalY=0 NormalZ=1 AngleXU=0 Radius=2 StartAngle=3.14159 EndAngle=4.71239
    g33: GeomPoint X=-20 Y=-15 Z=0
    g34: ArcOfCircle CenterX=-17 CenterY=-17 CenterZ=0 NormalX=0 NormalY=0 NormalZ=1 AngleXU=0 Radius=2 StartAngle=0 EndAngle=1.5708
    g35: GeomPoint X=-15 Y=-15 Z=0
  constraints (80):
    c: Horizontal(g2)
    c: Vertical(g3)
    c: Symmetric(g21,g31,g-2)
    c: Symmetric(g21,g19,g-1)
    c: DistanceX(g31,g21) = 40
    c: DistanceY(g19,g21) = 30
    c: Horizontal(g4)
    c: Vertical(g7)
    c: Symmetric(g13,g15,g-2)
    c: Symmetric(g15,g25,g-1)
    c: DistanceY(g15,g25) = 40
    c: Vertical(g9)
    c: Vertical(g5)
    c: Vertical(g11)
    c: Horizontal(g10)
    c: Horizontal(g8)
    c: Horizontal(g0)
    c: DistanceX(g13,g15) = 30
    c: DistanceY(g33,g31) = 30
    c: DistanceX(g27,g25) = 30
    c: PointOnObject(g13,g7)
    c: PointOnObject(g13,g6)
    c: Tangent(g7,g12) = 1.5708
    c: Tangent(g6,g12) = 1.5708
    c: Radius(g12) = 2
    c: PointOnObject(g15,g11)
    c: PointOnObject(g15,g6)
    c: Tangent(g11,g14) = 1.5708
    c: Tangent(g6,g14) = 1.5708
    c: PointOnObject(g17,g11)
    c: PointOnObject(g17,g2)
    c: Tangent(g11,g16) = -1.5708
    c: Tangent(g2,g16) = -1.5708
    c: PointOnObject(g19,g2)
    c: PointOnObject(g19,g1)
    c: Tangent(g2,g18) = 1.5708
    c: Tangent(g1,g18) = 1.5708
    c: PointOnObject(g21,g1)
    c: PointOnObject(g21,g8)
    c: Tangent(g1,g20) = 1.5708
    c: Tangent(g8,g20) = 1.5708
    c: PointOnObject(g23,g8)
    c: PointOnObject(g23,g5)
    c: Tangent(g8,g22) = -1.5708
    c: Tangent(g5,g22) = -1.5708
    c: PointOnObject(g25,g5)
    c: PointOnObject(g25,g4)
    c: Tangent(g5,g24) = 1.5708
    c: Tangent(g4,g24) = 1.5708
    c: PointOnObject(g27,g9)
    c: PointOnObject(g27,g4)
    c: Tangent(g9,g26) = 1.5708
    c: Tangent(g4,g26) = 1.5708
    c: PointOnObject(g29,g9)
    c: PointOnObject(g29,g0)
    c: Tangent(g9,g28) = -1.5708
    c: Tangent(g0,g28) = -1.5708
    c: PointOnObject(g31,g0)
    c: PointOnObject(g31,g3)
    c: Tangent(g0,g30) = 1.5708
    c: Tangent(g3,g30) = 1.5708
    c: PointOnObject(g33,g3)
    c: PointOnObject(g33,g10)
    c: Tangent(g3,g32) = 1.5708
    c: Tangent(g10,g32) = 1.5708
    c: PointOnObject(g35,g10)
    c: PointOnObject(g35,g7)
    c: Tangent(g10,g34) = -1.5708
    c: Tangent(g7,g34) = -1.5708
    c: Radius(g34) = 2
    c: Radius(g32) = 2
    c: Radius(g30) = 2
    c: Radius(g28) = 2
    c: Radius(g26) = 2
    c: Radius(g24) = 2
    c: Radius(g22) = 2
    c: Radius(g20) = 2
    c: Radius(g18) = 2
    c: Radius(g16) = 2
    c: Radius(g14) = 2
FEATURE [PartDesign::Pocket] Pocket035
  BaseFeature = -> Pad007
  Direction = (0,0,-1)
  Length = 5
  Length2 = 5
  Profile = -> Sketch042
  ReferenceAxis = -> Sketch042 [N_Axis]
  Type = 1
FEATURE [Sketcher::SketchObject] Sketch043
  ExternalGeometry = -> [Pocket035]
  FullyConstrained = true
  MapMode = 5
  Placement = pos=(25,0,0) rot=(0.57735,0.57735,0.57735;2.0944rad)
  Support = -> [Pocket035]
  sketch-geometry (6):
    g0: LineSegment StartX=-15 StartY=10 StartZ=0 EndX=15 EndY=10 EndZ=0
    g1: LineSegment StartX=20 StartY=5 StartZ=0 EndX=20 EndY=0 EndZ=0
    g2: LineSegment StartX=20 StartY=0 StartZ=0 EndX=-20 EndY=0 EndZ=0
    g3: LineSegment StartX=-20 StartY=0 StartZ=0 EndX=-20 EndY=5 EndZ=0
    g4: ArcOfCircle CenterX=15 CenterY=5 CenterZ=0 NormalX=0 NormalY=0 NormalZ=1 AngleXU=0 Radius=5 StartAngle=1.11001e-11 EndAngle=1.5708
    g5: ArcOfCircle CenterX=-15 CenterY=5 CenterZ=0 NormalX=0 NormalY=0 NormalZ=1 AngleXU=0 Radius=5 StartAngle=1.5708 EndAngle=3.14159
  constraints (15):
    c: Coincident(g1,g2)
    c: Coincident(g2,g3)
    c: Vertical(g1)
    c: Vertical(g3)
    c: PointOnObject(g1,g-1)
    c: Tangent(g1,g4) = 1.5708
    c: Tangent(g0,g4) = 1.5708
    c: Tangent(g0,g5) = 1.5708
    c: Tangent(g3,g5) = 1.5708
    c: Horizontal(g0)
    c: DistanceX(g2,g2) = 40
    c: Symmetric(g2,g1,g-2)
    c: Distance(g-1,g0) = 10
    c: Radius(g5) = 5
    c: Radius(g4) = 5
FEATURE [PartDesign::Pocket] Pocket036
  BaseFeature = -> Pocket035
  Direction = (-1,0,0)
  Length = 5
  Length2 = 5
  Profile = -> Sketch043
  ReferenceAxis = -> Sketch043 [N_Axis]
  Type = 1
FEATURE [Sketcher::SketchObject] Sketch044
  FullyConstrained = true
  MapMode = 5
  Placement = pos=(0,-25,0) rot=(1,0,0;1.5708rad)
  Support = -> [Pocket035]
  sketch-geometry (6):
    g0: LineSegment StartX=-15 StartY=10 StartZ=0 EndX=15 EndY=10 EndZ=0
    g1: LineSegment StartX=20 StartY=5 StartZ=0 EndX=20 EndY=0 EndZ=0
    g2: LineSegment StartX=20 StartY=0 StartZ=0 EndX=-20 EndY=0 EndZ=0
    g3: LineSegment StartX=-20 StartY=0 StartZ=0 EndX=-20 EndY=5 EndZ=0
    g4: ArcOfCircle CenterX=15 CenterY=5 CenterZ=0 NormalX=0 NormalY=0 NormalZ=1 AngleXU=0 Radius=5 StartAngle=1.11e-11 EndAngle=1.5708
    g5: ArcOfCircle CenterX=-15 CenterY=5 CenterZ=0 NormalX=0 NormalY=0 NormalZ=1 AngleXU=0 Radius=5 StartAngle=1.5708 EndAngle=3.14159
  constraints (15):
    c: Coincident(g1,g2)
    c: Coincident(g2,g3)
    c: Horizontal(g0)
    c: Vertical(g1)
    c: Vertical(g3)
    c: Symmetric(g2,g1,g-2)
    c: PointOnObject(g1,g-1)
    c: Tangent(g0,g4) = 1.5708
    c: Tangent(g1,g4) = 1.5708
    c: Tangent(g0,g5) = 1.5708
    c: Tangent(g3,g5) = 1.5708
    c: DistanceX(g2,g2) = 40
    c: Distance(g-1,g0) = 10
    c: Radius(g5) = 5
    c: Radius(g4) = 5
FEATURE [PartDesign::Pocket] Pocket037
  BaseFeature = -> Pocket036
  Direction = (0,1,-2e-16)
  Length = 5
  Length2 = 5
  Profile = -> Sketch044
  ReferenceAxis = -> Sketch044 [N_Axis]
  Type = 1
FEATURE [Sketcher::SketchObject] Sketch045
  FullyConstrained = false
  MapMode = 5
  Placement = pos=(0,0,20) rot=(0,0,1;0rad)
  sketch-geometry (4):
    g0: Circle CenterX=-20 CenterY=20 CenterZ=0 NormalX=0 NormalY=0 NormalZ=1 AngleXU=0 Radius=1.55
    g1: Circle CenterX=20 CenterY=20 CenterZ=0 NormalX=0 NormalY=0 NormalZ=1 AngleXU=0 Radius=1.55
    g2: Circle CenterX=20 CenterY=-20 CenterZ=0 NormalX=0 NormalY=0 NormalZ=1 AngleXU=0 Radius=1.55
    g3: Circle CenterX=-20 CenterY=-20 CenterZ=0 NormalX=0 NormalY=0 NormalZ=1 AngleXU=0 Radius=1.55
  constraints (4):
    c: Diameter(g0) = 3.1
    c: Diameter(g1) = 3.1
    c: Diameter(g2) = 3.1
    c: Diameter(g3) = 3.1
FEATURE [PartDesign::Pocket] Pocket038
  BaseFeature = -> Pocket037
  Direction = (0,0,-1)
  Length = 5
  Length2 = 5
  Profile = -> Sketch045
  ReferenceAxis = -> Sketch045 [N_Axis]
  Type = 0
FEATURE [Sketcher::SketchObject] Sketch046
  ExternalGeometry = -> [Pocket038]
  FullyConstrained = true
  MapMode = 5
  Placement = pos=(0,-25,0) rot=(1,0,0;1.5708rad)
  Support = -> [Pocket038]
  sketch-geometry (2):
    g0: Circle CenterX=-20 CenterY=14 CenterZ=0 NormalX=0 NormalY=0 NormalZ=1 AngleXU=0 Radius=1.55
    g1: Circle CenterX=20 CenterY=14 CenterZ=0 NormalX=0 NormalY=0 NormalZ=1 AngleXU=0 Radius=1.55
  constraints (6):
    c: Diameter(g0) = 3.1
    c: Diameter(g1) = 3.1
    c: Distance(g0,g-5) = 5
    c: Distance(g0,g-3) = 6
    c: Distance(g1,g-3) = 6
    c: Distance(g1,g-4) = 5
FEATURE [PartDesign::Pocket] Pocket039
  BaseFeature = -> Pocket038
  Direction = (0,1,-2e-16)
  Length = 3
  Length2 = 5
  Profile = -> Sketch046
  ReferenceAxis = -> Sketch046 [N_Axis]
  Type = 0
FEATURE [Sketcher::SketchObject] Sketch047
  ExternalGeometry = -> [Pocket039]
  FullyConstrained = true
  MapMode = 5
  Placement = pos=(-25,0,0) rot=(0.57735,-0.57735,-0.57735;2.0944rad)
  Support = -> [Pocket039]
  sketch-geometry (2):
    g0: Circle CenterX=-20 CenterY=14 CenterZ=0 NormalX=0 NormalY=0 NormalZ=1 AngleXU=0 Radius=1.4
    g1: Circle CenterX=20 CenterY=14 CenterZ=0 NormalX=0 NormalY=0 NormalZ=1 AngleXU=0 Radius=1.4
  constraints (6):
    c: Diameter(g0) = 2.8
    c: Diameter(g1) = 2.8
    c: Distance(g0,g-3) = 5
    c: Distance(g0,g-4) = 6
    c: Distance(g1,g-4) = 6
    c: Distance(g1,g-5) = 5
FEATURE [PartDesign::Pocket] Pocket040
  BaseFeature = -> Pocket039
  Direction = (1,0,0)
  Length = 3
  Length2 = 5
  Profile = -> Sketch047
  ReferenceAxis = -> Sketch047 [N_Axis]
  Type = 0
FEATURE [PartDesign::Body] Body008  label="BackplaneBlock006"
  Group = -> [Sketch041,Pad007,Sketch042,Pocket035,Sketch043,Sketch044,Pocket036,Pocket037,Sketch045,Pocket038,Sketch046,Pocket039,Sketch047,Pocket040]
  Origin = -> Origin008
  Placement = pos=(145,25,0) rot=(0,0,1;1.5708rad)
  Tip = -> Pocket040
FEATURE [Sketcher::SketchObject] Sketch048
  FullyConstrained = true
  MapMode = 5
  Support = -> [XY_Plane009]
  sketch-geometry (4):
    g0: LineSegment StartX=-25 StartY=25 StartZ=0 EndX=25 EndY=25 EndZ=0
    g1: LineSegment StartX=25 StartY=25 StartZ=0 EndX=25 EndY=-25 EndZ=0
    g2: LineSegment StartX=25 StartY=-25 StartZ=0 EndX=-25 EndY=-25 EndZ=0
    g3: LineSegment StartX=-25 StartY=-25 StartZ=0 EndX=-25 EndY=25 EndZ=0
  constraints (10):
    c: Coincident(g0,g1)
    c: Coincident(g1,g2)
    c: Coincident(g2,g3)
    c: Coincident(g3,g0)
    c: Horizontal(g0)
    c: Vertical(g3)
    c: Symmetric(g2,g1,g-2)
    c: Symmetric(g1,g0,g-1)
    c: DistanceY(g1,g1) = 50
    c: DistanceX(g2,g2) = 50
FEATURE [PartDesign::Pad] Pad008
  Direction = (0,0,1)
  Length = 20
  Length2 = 10
  Profile = -> Sketch048
  ReferenceAxis = -> Sketch048 [N_Axis]
  Type = 0
FEATURE [Sketcher::SketchObject] Sketch049
  ExternalGeometry = -> [Pad008]
  FullyConstrained = true
  MapMode = 5
  Placement = pos=(0,0,20) rot=(0,0,1;0rad)
  Support = -> [Pad008]
  sketch-geometry (36):
    g0: LineSegment StartX=-18 StartY=15 StartZ=0 EndX=-17 EndY=15 EndZ=0
    g1: LineSegment StartX=20 StartY=13 StartZ=0 EndX=20 EndY=-13 EndZ=0
    g2: LineSegment StartX=18 StartY=-15 StartZ=0 EndX=17 EndY=-15 EndZ=0
    g3: LineSegment StartX=-20 StartY=-13 StartZ=0 EndX=-20 EndY=13 EndZ=0
    g4: LineSegment StartX=-13 StartY=20 StartZ=0 EndX=13 EndY=20 EndZ=0
    g5: LineSegment StartX=15 StartY=18 StartZ=0 EndX=15 EndY=17 EndZ=0
    g6: LineSegment StartX=13 StartY=-20 StartZ=0 EndX=-13 EndY=-20 EndZ=0
    g7: LineSegment StartX=-15 StartY=-18 StartZ=0 EndX=-15 EndY=-17 EndZ=0
    g8: LineSegment StartX=17 StartY=15 StartZ=0 EndX=18 EndY=15 EndZ=0
    g9: LineSegment StartX=-15 StartY=17 StartZ=0 EndX=-15 EndY=18 EndZ=0
    g10: LineSegment StartX=-17 StartY=-15 StartZ=0 EndX=-18 EndY=-15 EndZ=0
    g11: LineSegment StartX=15 StartY=-17 StartZ=0 EndX=15 EndY=-18 EndZ=0
    g12: ArcOfCircle CenterX=-13 CenterY=-18 CenterZ=0 NormalX=0 NormalY=0 NormalZ=1 AngleXU=0 Radius=2 StartAngle=3.14159 EndAngle=4.71239
    g13: GeomPoint X=-15 Y=-20 Z=0
    g14: ArcOfCircle CenterX=13 CenterY=-18 CenterZ=0 NormalX=0 NormalY=0 NormalZ=1 AngleXU=0 Radius=2 StartAngle=4.71239 EndAngle=6.28319
    g15: GeomPoint X=15 Y=-20 Z=0
    g16: ArcOfCircle CenterX=17 CenterY=-17 CenterZ=0 NormalX=0 NormalY=0 NormalZ=1 AngleXU=0 Radius=2 StartAngle=1.5708 EndAngle=3.14159
    g17: GeomPoint X=15 Y=-15 Z=0
    g18: ArcOfCircle CenterX=18 CenterY=-13 CenterZ=0 NormalX=0 NormalY=0 NormalZ=1 AngleXU=0 Radius=2 StartAngle=4.71239 EndAngle=6.28319
    g19: GeomPoint X=20 Y=-15 Z=0
    g20: ArcOfCircle CenterX=18 CenterY=13 CenterZ=0 NormalX=0 NormalY=0 NormalZ=1 AngleXU=0 Radius=2 StartAngle=0 EndAngle=1.5708
    g21: GeomPoint X=20 Y=15 Z=0
    g22: ArcOfCircle CenterX=17 CenterY=17 CenterZ=0 NormalX=0 NormalY=0 NormalZ=1 AngleXU=0 Radius=2 StartAngle=3.14159 EndAngle=4.71239
    g23: GeomPoint X=15 Y=15 Z=0
    g24: ArcOfCircle CenterX=13 CenterY=18 CenterZ=0 NormalX=0 NormalY=0 NormalZ=1 AngleXU=0 Radius=2 StartAngle=4e-16 EndAngle=1.5708
    g25: GeomPoint X=15 Y=20 Z=0
    g26: ArcOfCircle CenterX=-13 CenterY=18 CenterZ=0 NormalX=0 NormalY=0 NormalZ=1 AngleXU=0 Radius=2 StartAngle=1.5708 EndAngle=3.14159
    g27: GeomPoint X=-15 Y=20 Z=0
    g28: ArcOfCircle CenterX=-17 CenterY=17 CenterZ=0 NormalX=0 NormalY=0 NormalZ=1 AngleXU=0 Radius=2 StartAngle=4.71239 EndAngle=6.28319
    g29: GeomPoint X=-15 Y=15 Z=0
    g30: ArcOfCircle CenterX=-18 CenterY=13 CenterZ=0 NormalX=0 NormalY=0 NormalZ=1 AngleXU=0 Radius=2 StartAngle=1.5708 EndAngle=3.14159
    g31: GeomPoint X=-20 Y=15 Z=0
    g32: ArcOfCircle CenterX=-18 CenterY=-13 CenterZ=0 NormalX=0 NormalY=0 NormalZ=1 AngleXU=0 Radius=2 StartAngle=3.14159 EndAngle=4.71239
    g33: GeomPoint X=-20 Y=-15 Z=0
    g34: ArcOfCircle CenterX=-17 CenterY=-17 CenterZ=0 NormalX=0 NormalY=0 NormalZ=1 AngleXU=0 Radius=2 StartAngle=0 EndAngle=1.5708
    g35: GeomPoint X=-15 Y=-15 Z=0
  constraints (80):
    c: Horizontal(g2)
    c: Vertical(g3)
    c: Symmetric(g21,g31,g-2)
    c: Symmetric(g21,g19,g-1)
    c: DistanceX(g31,g21) = 40
    c: DistanceY(g19,g21) = 30
    c: Horizontal(g4)
    c: Vertical(g7)
    c: Symmetric(g13,g15,g-2)
    c: Symmetric(g15,g25,g-1)
    c: DistanceY(g15,g25) = 40
    c: Vertical(g9)
    c: Vertical(g5)
    c: Vertical(g11)
    c: Horizontal(g10)
    c: Horizontal(g8)
    c: Horizontal(g0)
    c: DistanceX(g13,g15) = 30
    c: DistanceY(g33,g31) = 30
    c: DistanceX(g27,g25) = 30
    c: PointOnObject(g13,g7)
    c: PointOnObject(g13,g6)
    c: Tangent(g7,g12) = 1.5708
    c: Tangent(g6,g12) = 1.5708
    c: Radius(g12) = 2
    c: PointOnObject(g15,g11)
    c: PointOnObject(g15,g6)
    c: Tangent(g11,g14) = 1.5708
    c: Tangent(g6,g14) = 1.5708
    c: PointOnObject(g17,g11)
    c: PointOnObject(g17,g2)
    c: Tangent(g11,g16) = -1.5708
    c: Tangent(g2,g16) = -1.5708
    c: PointOnObject(g19,g2)
    c: PointOnObject(g19,g1)
    c: Tangent(g2,g18) = 1.5708
    c: Tangent(g1,g18) = 1.5708
    c: PointOnObject(g21,g1)
    c: PointOnObject(g21,g8)
    c: Tangent(g1,g20) = 1.5708
    c: Tangent(g8,g20) = 1.5708
    c: PointOnObject(g23,g8)
    c: PointOnObject(g23,g5)
    c: Tangent(g8,g22) = -1.5708
    c: Tangent(g5,g22) = -1.5708
    c: PointOnObject(g25,g5)
    c: PointOnObject(g25,g4)
    c: Tangent(g5,g24) = 1.5708
    c: Tangent(g4,g24) = 1.5708
    c: PointOnObject(g27,g9)
    c: PointOnObject(g27,g4)
    c: Tangent(g9,g26) = 1.5708
    c: Tangent(g4,g26) = 1.5708
    c: PointOnObject(g29,g9)
    c: PointOnObject(g29,g0)
    c: Tangent(g9,g28) = -1.5708
    c: Tangent(g0,g28) = -1.5708
    c: PointOnObject(g31,g0)
    c: PointOnObject(g31,g3)
    c: Tangent(g0,g30) = 1.5708
    c: Tangent(g3,g30) = 1.5708
    c: PointOnObject(g33,g3)
    c: PointOnObject(g33,g10)
    c: Tangent(g3,g32) = 1.5708
    c: Tangent(g10,g32) = 1.5708
    c: PointOnObject(g35,g10)
    c: PointOnObject(g35,g7)
    c: Tangent(g10,g34) = -1.5708
    c: Tangent(g7,g34) = -1.5708
    c: Radius(g34) = 2
    c: Radius(g32) = 2
    c: Radius(g30) = 2
    c: Radius(g28) = 2
    c: Radius(g26) = 2
    c: Radius(g24) = 2
    c: Radius(g22) = 2
    c: Radius(g20) = 2
    c: Radius(g18) = 2
    c: Radius(g16) = 2
    c: Radius(g14) = 2
FEATURE [PartDesign::Pocket] Pocket041
  BaseFeature = -> Pad008
  Direction = (0,0,-1)
  Length = 5
  Length2 = 5
  Profile = -> Sketch049
  ReferenceAxis = -> Sketch049 [N_Axis]
  Type = 1
FEATURE [Sketcher::SketchObject] Sketch050
  ExternalGeometry = -> [Pocket041]
  FullyConstrained = true
  MapMode = 5
  Placement = pos=(25,0,0) rot=(0.57735,0.57735,0.57735;2.0944rad)
  Support = -> [Pocket041]
  sketch-geometry (6):
    g0: LineSegment StartX=-15 StartY=10 StartZ=0 EndX=15 EndY=10 EndZ=0
    g1: LineSegment StartX=20 StartY=5 StartZ=0 EndX=20 EndY=0 EndZ=0
    g2: LineSegment StartX=20 StartY=0 StartZ=0 EndX=-20 EndY=0 EndZ=0
    g3: LineSegment StartX=-20 StartY=0 StartZ=0 EndX=-20 EndY=5 EndZ=0
    g4: ArcOfCircle CenterX=15 CenterY=5 CenterZ=0 NormalX=0 NormalY=0 NormalZ=1 AngleXU=0 Radius=5 StartAngle=1.11001e-11 EndAngle=1.5708
    g5: ArcOfCircle CenterX=-15 CenterY=5 CenterZ=0 NormalX=0 NormalY=0 NormalZ=1 AngleXU=0 Radius=5 StartAngle=1.5708 EndAngle=3.14159
  constraints (15):
    c: Coincident(g1,g2)
    c: Coincident(g2,g3)
    c: Vertical(g1)
    c: Vertical(g3)
    c: PointOnObject(g1,g-1)
    c: Tangent(g1,g4) = 1.5708
    c: Tangent(g0,g4) = 1.5708
    c: Tangent(g0,g5) = 1.5708
    c: Tangent(g3,g5) = 1.5708
    c: Horizontal(g0)
    c: DistanceX(g2,g2) = 40
    c: Symmetric(g2,g1,g-2)
    c: Distance(g-1,g0) = 10
    c: Radius(g5) = 5
    c: Radius(g4) = 5
FEATURE [PartDesign::Pocket] Pocket042
  BaseFeature = -> Pocket041
  Direction = (-1,0,0)
  Length = 5
  Length2 = 5
  Profile = -> Sketch050
  ReferenceAxis = -> Sketch050 [N_Axis]
  Type = 1
FEATURE [Sketcher::SketchObject] Sketch051
  FullyConstrained = true
  MapMode = 5
  Placement = pos=(0,-25,0) rot=(1,0,0;1.5708rad)
  Support = -> [Pocket041]
  sketch-geometry (6):
    g0: LineSegment StartX=-15 StartY=10 StartZ=0 EndX=15 EndY=10 EndZ=0
    g1: LineSegment StartX=20 StartY=5 StartZ=0 EndX=20 EndY=0 EndZ=0
    g2: LineSegment StartX=20 StartY=0 StartZ=0 EndX=-20 EndY=0 EndZ=0
    g3: LineSegment StartX=-20 StartY=0 StartZ=0 EndX=-20 EndY=5 EndZ=0
    g4: ArcOfCircle CenterX=15 CenterY=5 CenterZ=0 NormalX=0 NormalY=0 NormalZ=1 AngleXU=0 Radius=5 StartAngle=1.11e-11 EndAngle=1.5708
    g5: ArcOfCircle CenterX=-15 CenterY=5 CenterZ=0 NormalX=0 NormalY=0 NormalZ=1 AngleXU=0 Radius=5 StartAngle=1.5708 EndAngle=3.14159
  constraints (15):
    c: Coincident(g1,g2)
    c: Coincident(g2,g3)
    c: Horizontal(g0)
    c: Vertical(g1)
    c: Vertical(g3)
    c: Symmetric(g2,g1,g-2)
    c: PointOnObject(g1,g-1)
    c: Tangent(g0,g4) = 1.5708
    c: Tangent(g1,g4) = 1.5708
    c: Tangent(g0,g5) = 1.5708
    c: Tangent(g3,g5) = 1.5708
    c: DistanceX(g2,g2) = 40
    c: Distance(g-1,g0) = 10
    c: Radius(g5) = 5
    c: Radius(g4) = 5
FEATURE [PartDesign::Pocket] Pocket043
  BaseFeature = -> Pocket042
  Direction = (0,1,-2e-16)
  Length = 5
  Length2 = 5
  Profile = -> Sketch051
  ReferenceAxis = -> Sketch051 [N_Axis]
  Type = 1
FEATURE [Sketcher::SketchObject] Sketch052
  FullyConstrained = false
  MapMode = 5
  Placement = pos=(0,0,20) rot=(0,0,1;0rad)
  sketch-geometry (4):
    g0: Circle CenterX=-20 CenterY=20 CenterZ=0 NormalX=0 NormalY=0 NormalZ=1 AngleXU=0 Radius=1.55
    g1: Circle CenterX=20 CenterY=20 CenterZ=0 NormalX=0 NormalY=0 NormalZ=1 AngleXU=0 Radius=1.55
    g2: Circle CenterX=20 CenterY=-20 CenterZ=0 NormalX=0 NormalY=0 NormalZ=1 AngleXU=0 Radius=1.55
    g3: Circle CenterX=-20 CenterY=-20 CenterZ=0 NormalX=0 NormalY=0 NormalZ=1 AngleXU=0 Radius=1.55
  constraints (4):
    c: Diameter(g0) = 3.1
    c: Diameter(g1) = 3.1
    c: Diameter(g2) = 3.1
    c: Diameter(g3) = 3.1
FEATURE [PartDesign::Pocket] Pocket044
  BaseFeature = -> Pocket043
  Direction = (0,0,-1)
  Length = 5
  Length2 = 5
  Profile = -> Sketch052
  ReferenceAxis = -> Sketch052 [N_Axis]
  Type = 0
FEATURE [Sketcher::SketchObject] Sketch053
  ExternalGeometry = -> [Pocket044]
  FullyConstrained = true
  MapMode = 5
  Placement = pos=(0,-25,0) rot=(1,0,0;1.5708rad)
  Support = -> [Pocket044]
  sketch-geometry (2):
    g0: Circle CenterX=-20 CenterY=14 CenterZ=0 NormalX=0 NormalY=0 NormalZ=1 AngleXU=0 Radius=1.4
    g1: Circle CenterX=20 CenterY=14 CenterZ=0 NormalX=0 NormalY=0 NormalZ=1 AngleXU=0 Radius=1.4
  constraints (6):
    c: Diameter(g0) = 2.8
    c: Diameter(g1) = 2.8
    c: Distance(g0,g-5) = 5
    c: Distance(g0,g-3) = 6
    c: Distance(g1,g-3) = 6
    c: Distance(g1,g-4) = 5
FEATURE [PartDesign::Pocket] Pocket045
  BaseFeature = -> Pocket044
  Direction = (0,1,-2e-16)
  Length = 3
  Length2 = 5
  Profile = -> Sketch053
  ReferenceAxis = -> Sketch053 [N_Axis]
  Type = 0
FEATURE [Sketcher::SketchObject] Sketch054
  ExternalGeometry = -> [Pocket045]
  FullyConstrained = true
  MapMode = 5
  Placement = pos=(-25,0,0) rot=(0.57735,-0.57735,-0.57735;2.0944rad)
  Support = -> [Pocket045]
  sketch-geometry (2):
    g0: Circle CenterX=-20 CenterY=14 CenterZ=0 NormalX=0 NormalY=0 NormalZ=1 AngleXU=0 Radius=1.4
    g1: Circle CenterX=20 CenterY=14 CenterZ=0 NormalX=0 NormalY=0 NormalZ=1 AngleXU=0 Radius=1.4
  constraints (6):
    c: Diameter(g0) = 2.8
    c: Diameter(g1) = 2.8
    c: Distance(g0,g-3) = 5
    c: Distance(g0,g-4) = 6
    c: Distance(g1,g-4) = 6
    c: Distance(g1,g-5) = 5
FEATURE [PartDesign::Pocket] Pocket046
  BaseFeature = -> Pocket045
  Direction = (1,0,0)
  Length = 3
  Length2 = 5
  Profile = -> Sketch054
  ReferenceAxis = -> Sketch054 [N_Axis]
  Type = 0
FEATURE [PartDesign::Body] Body009  label="BackplaneBlock007"
  Group = -> [Sketch048,Pad008,Sketch049,Pocket041,Sketch050,Sketch051,Pocket042,Pocket043,Sketch052,Pocket044,Sketch053,Pocket045,Sketch054,Pocket046]
  Origin = -> Origin009
  Placement = pos=(25,145,0) rot=(0,0,-1;1.5708rad)
  Tip = -> Pocket046
FEATURE [Sketcher::SketchObject] Sketch055
  FullyConstrained = true
  MapMode = 5
  Support = -> [XY_Plane010]
  sketch-geometry (4):
    g0: LineSegment StartX=-25 StartY=25 StartZ=0 EndX=25 EndY=25 EndZ=0
    g1: LineSegment StartX=25 StartY=25 StartZ=0 EndX=25 EndY=-25 EndZ=0
    g2: LineSegment StartX=25 StartY=-25 StartZ=0 EndX=-25 EndY=-25 EndZ=0
    g3: LineSegment StartX=-25 StartY=-25 StartZ=0 EndX=-25 EndY=25 EndZ=0
  constraints (10):
    c: Coincident(g0,g1)
    c: Coincident(g1,g2)
    c: Coincident(g2,g3)
    c: Coincident(g3,g0)
    c: Horizontal(g0)
    c: Vertical(g3)
    c: Symmetric(g2,g1,g-2)
    c: Symmetric(g1,g0,g-1)
    c: DistanceY(g1,g1) = 50
    c: DistanceX(g2,g2) = 50
FEATURE [PartDesign::Pad] Pad009
  Direction = (0,0,1)
  Length = 20
  Length2 = 10
  Profile = -> Sketch055
  ReferenceAxis = -> Sketch055 [N_Axis]
  Type = 0
FEATURE [Sketcher::SketchObject] Sketch056
  ExternalGeometry = -> [Pad009]
  FullyConstrained = true
  MapMode = 5
  Placement = pos=(0,0,20) rot=(0,0,1;0rad)
  Support = -> [Pad009]
  sketch-geometry (36):
    g0: LineSegment StartX=-18 StartY=15 StartZ=0 EndX=-17 EndY=15 EndZ=0
    g1: LineSegment StartX=20 StartY=13 StartZ=0 EndX=20 EndY=-13 EndZ=0
    g2: LineSegment StartX=18 StartY=-15 StartZ=0 EndX=17 EndY=-15 EndZ=0
    g3: LineSegment StartX=-20 StartY=-13 StartZ=0 EndX=-20 EndY=13 EndZ=0
    g4: LineSegment StartX=-13 StartY=20 StartZ=0 EndX=13 EndY=20 EndZ=0
    g5: LineSegment StartX=15 StartY=18 StartZ=0 EndX=15 EndY=17 EndZ=0
    g6: LineSegment StartX=13 StartY=-20 StartZ=0 EndX=-13 EndY=-20 EndZ=0
    g7: LineSegment StartX=-15 StartY=-18 StartZ=0 EndX=-15 EndY=-17 EndZ=0
    g8: LineSegment StartX=17 StartY=15 StartZ=0 EndX=18 EndY=15 EndZ=0
    g9: LineSegment StartX=-15 StartY=17 StartZ=0 EndX=-15 EndY=18 EndZ=0
    g10: LineSegment StartX=-17 StartY=-15 StartZ=0 EndX=-18 EndY=-15 EndZ=0
    g11: LineSegment StartX=15 StartY=-17 StartZ=0 EndX=15 EndY=-18 EndZ=0
    g12: ArcOfCircle CenterX=-13 CenterY=-18 CenterZ=0 NormalX=0 NormalY=0 NormalZ=1 AngleXU=0 Radius=2 StartAngle=3.14159 EndAngle=4.71239
    g13: GeomPoint X=-15 Y=-20 Z=0
    g14: ArcOfCircle CenterX=13 CenterY=-18 CenterZ=0 NormalX=0 NormalY=0 NormalZ=1 AngleXU=0 Radius=2 StartAngle=4.71239 EndAngle=6.28319
    g15: GeomPoint X=15 Y=-20 Z=0
    g16: ArcOfCircle CenterX=17 CenterY=-17 CenterZ=0 NormalX=0 NormalY=0 NormalZ=1 AngleXU=0 Radius=2 StartAngle=1.5708 EndAngle=3.14159
    g17: GeomPoint X=15 Y=-15 Z=0
    g18: ArcOfCircle CenterX=18 CenterY=-13 CenterZ=0 NormalX=0 NormalY=0 NormalZ=1 AngleXU=0 Radius=2 StartAngle=4.71239 EndAngle=6.28319
    g19: GeomPoint X=20 Y=-15 Z=0
    g20: ArcOfCircle CenterX=18 CenterY=13 CenterZ=0 NormalX=0 NormalY=0 NormalZ=1 AngleXU=0 Radius=2 StartAngle=0 EndAngle=1.5708
    g21: GeomPoint X=20 Y=15 Z=0
    g22: ArcOfCircle CenterX=17 CenterY=17 CenterZ=0 NormalX=0 NormalY=0 NormalZ=1 AngleXU=0 Radius=2 StartAngle=3.14159 EndAngle=4.71239
    g23: GeomPoint X=15 Y=15 Z=0
    g24: ArcOfCircle CenterX=13 CenterY=18 CenterZ=0 NormalX=0 NormalY=0 NormalZ=1 AngleXU=0 Radius=2 StartAngle=4e-16 EndAngle=1.5708
    g25: GeomPoint X=15 Y=20 Z=0
    g26: ArcOfCircle CenterX=-13 CenterY=18 CenterZ=0 NormalX=0 NormalY=0 NormalZ=1 AngleXU=0 Radius=2 StartAngle=1.5708 EndAngle=3.14159
    g27: GeomPoint X=-15 Y=20 Z=0
    g28: ArcOfCircle CenterX=-17 CenterY=17 CenterZ=0 NormalX=0 NormalY=0 NormalZ=1 AngleXU=0 Radius=2 StartAngle=4.71239 EndAngle=6.28319
    g29: GeomPoint X=-15 Y=15 Z=0
    g30: ArcOfCircle CenterX=-18 CenterY=13 CenterZ=0 NormalX=0 NormalY=0 NormalZ=1 AngleXU=0 Radius=2 StartAngle=1.5708 EndAngle=3.14159
    g31: GeomPoint X=-20 Y=15 Z=0
    g32: ArcOfCircle CenterX=-18 CenterY=-13 CenterZ=0 NormalX=0 NormalY=0 NormalZ=1 AngleXU=0 Radius=2 StartAngle=3.14159 EndAngle=4.71239
    g33: GeomPoint X=-20 Y=-15 Z=0
    g34: ArcOfCircle CenterX=-17 CenterY=-17 CenterZ=0 NormalX=0 NormalY=0 NormalZ=1 AngleXU=0 Radius=2 StartAngle=0 EndAngle=1.5708
    g35: GeomPoint X=-15 Y=-15 Z=0
  constraints (80):
    c: Horizontal(g2)
    c: Vertical(g3)
    c: Symmetric(g21,g31,g-2)
    c: Symmetric(g21,g19,g-1)
    c: DistanceX(g31,g21) = 40
    c: DistanceY(g19,g21) = 30
    c: Horizontal(g4)
    c: Vertical(g7)
    c: Symmetric(g13,g15,g-2)
    c: Symmetric(g15,g25,g-1)
    c: DistanceY(g15,g25) = 40
    c: Vertical(g9)
    c: Vertical(g5)
    c: Vertical(g11)
    c: Horizontal(g10)
    c: Horizontal(g8)
    c: Horizontal(g0)
    c: DistanceX(g13,g15) = 30
    c: DistanceY(g33,g31) = 30
    c: DistanceX(g27,g25) = 30
    c: PointOnObject(g13,g7)
    c: PointOnObject(g13,g6)
    c: Tangent(g7,g12) = 1.5708
    c: Tangent(g6,g12) = 1.5708
    c: Radius(g12) = 2
    c: PointOnObject(g15,g11)
    c: PointOnObject(g15,g6)
    c: Tangent(g11,g14) = 1.5708
    c: Tangent(g6,g14) = 1.5708
    c: PointOnObject(g17,g11)
    c: PointOnObject(g17,g2)
    c: Tangent(g11,g16) = -1.5708
    c: Tangent(g2,g16) = -1.5708
    c: PointOnObject(g19,g2)
    c: PointOnObject(g19,g1)
    c: Tangent(g2,g18) = 1.5708
    c: Tangent(g1,g18) = 1.5708
    c: PointOnObject(g21,g1)
    c: PointOnObject(g21,g8)
    c: Tangent(g1,g20) = 1.5708
    c: Tangent(g8,g20) = 1.5708
    c: PointOnObject(g23,g8)
    c: PointOnObject(g23,g5)
    c: Tangent(g8,g22) = -1.5708
    c: Tangent(g5,g22) = -1.5708
    c: PointOnObject(g25,g5)
    c: PointOnObject(g25,g4)
    c: Tangent(g5,g24) = 1.5708
    c: Tangent(g4,g24) = 1.5708
    c: PointOnObject(g27,g9)
    c: PointOnObject(g27,g4)
    c: Tangent(g9,g26) = 1.5708
    c: Tangent(g4,g26) = 1.5708
    c: PointOnObject(g29,g9)
    c: PointOnObject(g29,g0)
    c: Tangent(g9,g28) = -1.5708
    c: Tangent(g0,g28) = -1.5708
    c: PointOnObject(g31,g0)
    c: PointOnObject(g31,g3)
    c: Tangent(g0,g30) = 1.5708
    c: Tangent(g3,g30) = 1.5708
    c: PointOnObject(g33,g3)
    c: PointOnObject(g33,g10)
    c: Tangent(g3,g32) = 1.5708
    c: Tangent(g10,g32) = 1.5708
    c: PointOnObject(g35,g10)
    c: PointOnObject(g35,g7)
    c: Tangent(g10,g34) = -1.5708
    c: Tangent(g7,g34) = -1.5708
    c: Radius(g34) = 2
    c: Radius(g32) = 2
    c: Radius(g30) = 2
    c: Radius(g28) = 2
    c: Radius(g26) = 2
    c: Radius(g24) = 2
    c: Radius(g22) = 2
    c: Radius(g20) = 2
    c: Radius(g18) = 2
    c: Radius(g16) = 2
    c: Radius(g14) = 2
FEATURE [PartDesign::Pocket] Pocket047
  BaseFeature = -> Pad009
  Direction = (0,0,-1)
  Length = 5
  Length2 = 5
  Profile = -> Sketch056
  ReferenceAxis = -> Sketch056 [N_Axis]
  Type = 1
FEATURE [Sketcher::SketchObject] Sketch057
  ExternalGeometry = -> [Pocket047]
  FullyConstrained = true
  MapMode = 5
  Placement = pos=(25,0,0) rot=(0.57735,0.57735,0.57735;2.0944rad)
  Support = -> [Pocket047]
  sketch-geometry (6):
    g0: LineSegment StartX=-15 StartY=10 StartZ=0 EndX=15 EndY=10 EndZ=0
    g1: LineSegment StartX=20 StartY=5 StartZ=0 EndX=20 EndY=0 EndZ=0
    g2: LineSegment StartX=20 StartY=0 StartZ=0 EndX=-20 EndY=0 EndZ=0
    g3: LineSegment StartX=-20 StartY=0 StartZ=0 EndX=-20 EndY=5 EndZ=0
    g4: ArcOfCircle CenterX=15 CenterY=5 CenterZ=0 NormalX=0 NormalY=0 NormalZ=1 AngleXU=0 Radius=5 StartAngle=1.11001e-11 EndAngle=1.5708
    g5: ArcOfCircle CenterX=-15 CenterY=5 CenterZ=0 NormalX=0 NormalY=0 NormalZ=1 AngleXU=0 Radius=5 StartAngle=1.5708 EndAngle=3.14159
  constraints (15):
    c: Coincident(g1,g2)
    c: Coincident(g2,g3)
    c: Vertical(g1)
    c: Vertical(g3)
    c: PointOnObject(g1,g-1)
    c: Tangent(g1,g4) = 1.5708
    c: Tangent(g0,g4) = 1.5708
    c: Tangent(g0,g5) = 1.5708
    c: Tangent(g3,g5) = 1.5708
    c: Horizontal(g0)
    c: DistanceX(g2,g2) = 40
    c: Symmetric(g2,g1,g-2)
    c: Distance(g-1,g0) = 10
    c: Radius(g5) = 5
    c: Radius(g4) = 5
FEATURE [PartDesign::Pocket] Pocket048
  BaseFeature = -> Pocket047
  Direction = (-1,0,0)
  Length = 5
  Length2 = 5
  Profile = -> Sketch057
  ReferenceAxis = -> Sketch057 [N_Axis]
  Type = 1
FEATURE [Sketcher::SketchObject] Sketch058
  FullyConstrained = true
  MapMode = 5
  Placement = pos=(0,-25,0) rot=(1,0,0;1.5708rad)
  Support = -> [Pocket047]
  sketch-geometry (6):
    g0: LineSegment StartX=-15 StartY=10 StartZ=0 EndX=15 EndY=10 EndZ=0
    g1: LineSegment StartX=20 StartY=5 StartZ=0 EndX=20 EndY=0 EndZ=0
    g2: LineSegment StartX=20 StartY=0 StartZ=0 EndX=-20 EndY=0 EndZ=0
    g3: LineSegment StartX=-20 StartY=0 StartZ=0 EndX=-20 EndY=5 EndZ=0
    g4: ArcOfCircle CenterX=15 CenterY=5 CenterZ=0 NormalX=0 NormalY=0 NormalZ=1 AngleXU=0 Radius=5 StartAngle=1.11e-11 EndAngle=1.5708
    g5: ArcOfCircle CenterX=-15 CenterY=5 CenterZ=0 NormalX=0 NormalY=0 NormalZ=1 AngleXU=0 Radius=5 StartAngle=1.5708 EndAngle=3.14159
  constraints (15):
    c: Coincident(g1,g2)
    c: Coincident(g2,g3)
    c: Horizontal(g0)
    c: Vertical(g1)
    c: Vertical(g3)
    c: Symmetric(g2,g1,g-2)
    c: PointOnObject(g1,g-1)
    c: Tangent(g0,g4) = 1.5708
    c: Tangent(g1,g4) = 1.5708
    c: Tangent(g0,g5) = 1.5708
    c: Tangent(g3,g5) = 1.5708
    c: DistanceX(g2,g2) = 40
    c: Distance(g-1,g0) = 10
    c: Radius(g5) = 5
    c: Radius(g4) = 5
FEATURE [PartDesign::Pocket] Pocket049
  BaseFeature = -> Pocket048
  Direction = (0,1,-2e-16)
  Length = 5
  Length2 = 5
  Profile = -> Sketch058
  ReferenceAxis = -> Sketch058 [N_Axis]
  Type = 1
FEATURE [Sketcher::SketchObject] Sketch059
  FullyConstrained = false
  MapMode = 5
  Placement = pos=(0,0,20) rot=(0,0,1;0rad)
  sketch-geometry (4):
    g0: Circle CenterX=-20 CenterY=20 CenterZ=0 NormalX=0 NormalY=0 NormalZ=1 AngleXU=0 Radius=1.55
    g1: Circle CenterX=20 CenterY=20 CenterZ=0 NormalX=0 NormalY=0 NormalZ=1 AngleXU=0 Radius=1.55
    g2: Circle CenterX=20 CenterY=-20 CenterZ=0 NormalX=0 NormalY=0 NormalZ=1 AngleXU=0 Radius=1.55
    g3: Circle CenterX=-20 CenterY=-20 CenterZ=0 NormalX=0 NormalY=0 NormalZ=1 AngleXU=0 Radius=1.55
  constraints (4):
    c: Diameter(g0) = 3.1
    c: Diameter(g1) = 3.1
    c: Diameter(g2) = 3.1
    c: Diameter(g3) = 3.1
FEATURE [PartDesign::Pocket] Pocket050
  BaseFeature = -> Pocket049
  Direction = (0,0,-1)
  Length = 5
  Length2 = 5
  Profile = -> Sketch059
  ReferenceAxis = -> Sketch059 [N_Axis]
  Type = 0
FEATURE [Sketcher::SketchObject] Sketch060
  ExternalGeometry = -> [Pocket050]
  FullyConstrained = true
  MapMode = 5
  Placement = pos=(0,-25,0) rot=(1,0,0;1.5708rad)
  Support = -> [Pocket050]
  sketch-geometry (2):
    g0: Circle CenterX=-20 CenterY=14 CenterZ=0 NormalX=0 NormalY=0 NormalZ=1 AngleXU=0 Radius=1.4
    g1: Circle CenterX=20 CenterY=14 CenterZ=0 NormalX=0 NormalY=0 NormalZ=1 AngleXU=0 Radius=1.4
  constraints (6):
    c: Diameter(g0) = 2.8
    c: Diameter(g1) = 2.8
    c: Distance(g0,g-5) = 5
    c: Distance(g0,g-3) = 6
    c: Distance(g1,g-3) = 6
    c: Distance(g1,g-4) = 5
FEATURE [PartDesign::Pocket] Pocket051
  BaseFeature = -> Pocket050
  Direction = (0,1,-2e-16)
  Length = 3
  Length2 = 5
  Profile = -> Sketch060
  ReferenceAxis = -> Sketch060 [N_Axis]
  Type = 0
FEATURE [Sketcher::SketchObject] Sketch061
  ExternalGeometry = -> [Pocket051]
  FullyConstrained = true
  MapMode = 5
  Placement = pos=(-25,0,0) rot=(0.57735,-0.57735,-0.57735;2.0944rad)
  Support = -> [Pocket051]
  sketch-geometry (2):
    g0: Circle CenterX=-20 CenterY=14 CenterZ=0 NormalX=0 NormalY=0 NormalZ=1 AngleXU=0 Radius=1.4
    g1: Circle CenterX=20 CenterY=14 CenterZ=0 NormalX=0 NormalY=0 NormalZ=1 AngleXU=0 Radius=1.4
  constraints (6):
    c: Diameter(g0) = 2.8
    c: Diameter(g1) = 2.8
    c: Distance(g0,g-3) = 5
    c: Distance(g0,g-4) = 6
    c: Distance(g1,g-4) = 6
    c: Distance(g1,g-5) = 5
FEATURE [PartDesign::Pocket] Pocket052
  BaseFeature = -> Pocket051
  Direction = (1,0,0)
  Length = 3
  Length2 = 5
  Profile = -> Sketch061
  ReferenceAxis = -> Sketch061 [N_Axis]
  Type = 0
FEATURE [PartDesign::Body] Body010  label="BackplaneBlock008"
  Group = -> [Sketch055,Pad009,Sketch056,Pocket047,Sketch057,Sketch058,Pocket048,Pocket049,Sketch059,Pocket050,Sketch060,Pocket051,Sketch061,Pocket052]
  Origin = -> Origin010
  Placement = pos=(145,145,0) rot=(0,0,1;3.14159rad)
  Tip = -> Pocket052
FEATURE [Part::Box] Box  label="Cube"
  AttacherType = Attacher::AttachEngine3D
  Height = 2
  Length = 10
  Placement = pos=(-10,0,18) rot=(0,0,1;0rad)
  Width = 50
FEATURE [Part::Cylinder] Cylinder
  Angle = 360
  AttacherType = Attacher::AttachEngine3D
  FirstAngle = 0
  Height = 10
  Placement = pos=(-5,12,14) rot=(0,0,1;0rad)
  Radius = 1.55
  SecondAngle = 0
FEATURE [Part::Cylinder] Cylinder001
  Angle = 360
  AttacherType = Attacher::AttachEngine3D
  FirstAngle = 0
  Height = 10
  Placement = pos=(-5,38,14) rot=(0,0,1;0rad)
  Radius = 1.55
  SecondAngle = 0
FEATURE [Part::Cut] Cut
  Base = -> Box
  Tool = -> Cylinder
FEATURE [Part::Cut] Cut001  label="Lip"
  Base = -> Cut
  Tool = -> Cylinder001
FEATURE [App::Link] Link  label="Lip001"
  LinkPlacement = pos=(0,60,0) rot=(0,0,1;0rad)
  LinkedObject = -> Cut001
  Placement = pos=(0,60,0) rot=(0,0,1;0rad)
FEATURE [App::Link] Link019  label="Lip002"
  LinkPlacement = pos=(0,120,0) rot=(0,0,1;0rad)
  LinkedObject = -> Cut001
  Placement = pos=(0,120,0) rot=(0,0,1;0rad)
FEATURE [App::Link] Link020  label="Lip003"
  LinkPlacement = pos=(0,170,0) rot=(0,0,1;4.71239rad)
  LinkedObject = -> Cut001
  Placement = pos=(0,170,0) rot=(0,0,1;4.71239rad)
FEATURE [App::Link] Link021  label="Lip004"
  LinkPlacement = pos=(60,170,0) rot=(0,0,1;4.71239rad)
  LinkedObject = -> Cut001
  Placement = pos=(60,170,0) rot=(0,0,1;4.71239rad)
FEATURE [App::Link] Link022  label="Lip005"
  LinkPlacement = pos=(120,170,0) rot=(0,0,1;4.71239rad)
  LinkedObject = -> Cut001
  Placement = pos=(120,170,0) rot=(0,0,1;4.71239rad)
FEATURE [App::Part] Part
  Group = -> [Body,Link008,Link009,Link010,Link011,Link012,Link013,Link014,Link015,Link016,Link017,Link018,Body002,Body003,Body004,Body005,Body006,Body007,Body008,Body009,Body010,Box,Cylinder,Cylinder001,Cut,Cut001,Link,Link019,Link020,Link021,Link022]
  Origin = -> Origin
FEATURE [Part::MultiFuse] Fusion
  Shapes = -> [Body,Link008,Link009,Link010,Link011,Link012,Link013,Link014,Link015,Link016,Link017,Link018,Body002,Body003,Body004,Body005,Body006,Body007,Body008,Body009,Body010,Cut001,Link,Link019,Link020,Link021,Link022]
FEATURE [Mesh::Feature] Mesh  label="Fusion (Meshed)"
